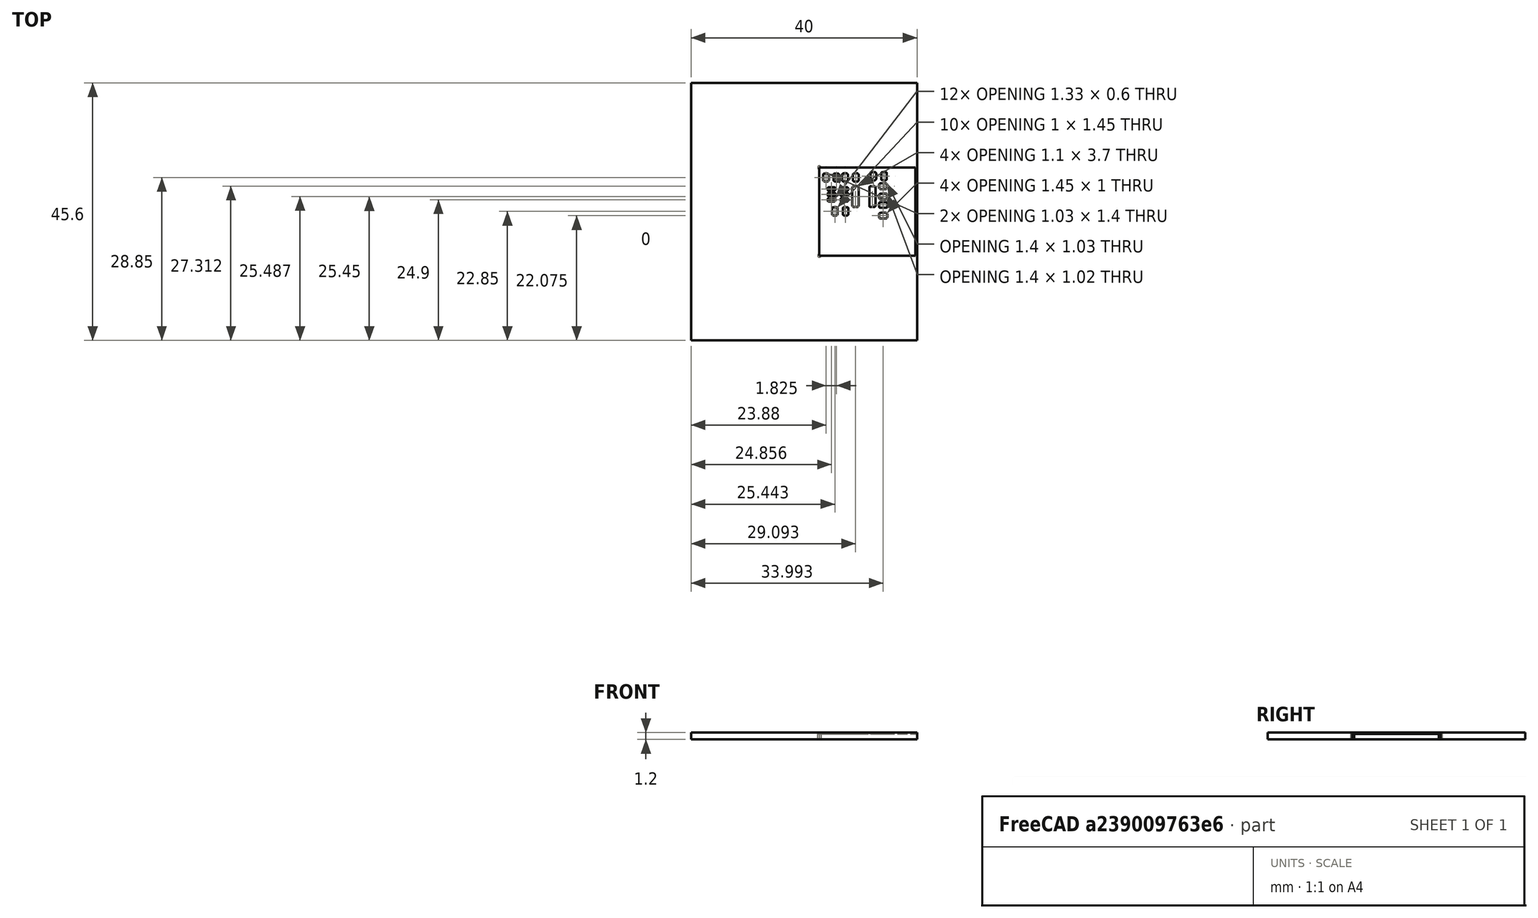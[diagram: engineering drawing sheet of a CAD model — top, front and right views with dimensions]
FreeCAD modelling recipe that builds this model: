
FCSTD DOCUMENT  (FreeCAD 1.0R39319 (Git))
Label: stencil
License: All rights reserved
LicenseURL: https://en.wikipedia.org/wiki/All_rights_reserved
objects: Sketcher::SketchObject×3, Part::Extrusion×3, Part::Box×1, Part::MultiFuse×1
note: 11 computed .brp shape members not serialized (recipe doc carries the construction recipe); baked Part::Feature solids carry a one-line shape summary decoded from their .brp

FEATURE [Part::Box] Box  label="Cover"
  AttacherType = Attacher::AttachEngine3D
  Height = 0.2
  Length = 2
  Placement = pos=(146.75,-81,0) rot=(0,0,1;0rad)
  Width = 17
FEATURE [Sketcher::SketchObject] Sketch
  ArcFitTolerance = 1e-06
  FullyConstrained = false
  MakeInternals = false
  sketch-geometry (284):
    g0: BSplineCurve PolesCount=2 KnotsCount=2 Degree=1 IsPeriodic=0
    g1: BSplineCurve PolesCount=2 KnotsCount=2 Degree=1 IsPeriodic=0
    g2: BSplineCurve PolesCount=2 KnotsCount=2 Degree=1 IsPeriodic=0
    g3: BSplineCurve PolesCount=2 KnotsCount=2 Degree=1 IsPeriodic=0
    g4: BSplineCurve PolesCount=2 KnotsCount=2 Degree=1 IsPeriodic=0
    g5: BSplineCurve PolesCount=2 KnotsCount=2 Degree=1 IsPeriodic=0
    g6: BSplineCurve PolesCount=2 KnotsCount=2 Degree=1 IsPeriodic=0
    g7: BSplineCurve PolesCount=2 KnotsCount=2 Degree=1 IsPeriodic=0
    g8: BSplineCurve PolesCount=2 KnotsCount=2 Degree=1 IsPeriodic=0
    g9: BSplineCurve PolesCount=2 KnotsCount=2 Degree=1 IsPeriodic=0
    g10: BSplineCurve PolesCount=2 KnotsCount=2 Degree=1 IsPeriodic=0
    g11: BSplineCurve PolesCount=2 KnotsCount=2 Degree=1 IsPeriodic=0
    g12: BSplineCurve PolesCount=2 KnotsCount=2 Degree=1 IsPeriodic=0
    g13: BSplineCurve PolesCount=2 KnotsCount=2 Degree=1 IsPeriodic=0
    g14: BSplineCurve PolesCount=2 KnotsCount=2 Degree=1 IsPeriodic=0
    g15: BSplineCurve PolesCount=2 KnotsCount=2 Degree=1 IsPeriodic=0
    g16: BSplineCurve PolesCount=2 KnotsCount=2 Degree=1 IsPeriodic=0
    g17: BSplineCurve PolesCount=2 KnotsCount=2 Degree=1 IsPeriodic=0
    g18: BSplineCurve PolesCount=2 KnotsCount=2 Degree=1 IsPeriodic=0
    g19: BSplineCurve PolesCount=2 KnotsCount=2 Degree=1 IsPeriodic=0
    g20: BSplineCurve PolesCount=2 KnotsCount=2 Degree=1 IsPeriodic=0
    g21: BSplineCurve PolesCount=2 KnotsCount=2 Degree=1 IsPeriodic=0
    g22: BSplineCurve PolesCount=2 KnotsCount=2 Degree=1 IsPeriodic=0
    g23: BSplineCurve PolesCount=2 KnotsCount=2 Degree=1 IsPeriodic=0
    g24: BSplineCurve PolesCount=2 KnotsCount=2 Degree=1 IsPeriodic=0
    g25: BSplineCurve PolesCount=2 KnotsCount=2 Degree=1 IsPeriodic=0
    g26: BSplineCurve PolesCount=2 KnotsCount=2 Degree=1 IsPeriodic=0
    g27: BSplineCurve PolesCount=2 KnotsCount=2 Degree=1 IsPeriodic=0
    g28: BSplineCurve PolesCount=2 KnotsCount=2 Degree=1 IsPeriodic=0
    g29: BSplineCurve PolesCount=2 KnotsCount=2 Degree=1 IsPeriodic=0
    g30: BSplineCurve PolesCount=2 KnotsCount=2 Degree=1 IsPeriodic=0
    g31: BSplineCurve PolesCount=2 KnotsCount=2 Degree=1 IsPeriodic=0
    g32: BSplineCurve PolesCount=2 KnotsCount=2 Degree=1 IsPeriodic=0
    g33: BSplineCurve PolesCount=2 KnotsCount=2 Degree=1 IsPeriodic=0
    g34: BSplineCurve PolesCount=2 KnotsCount=2 Degree=1 IsPeriodic=0
    g35: BSplineCurve PolesCount=2 KnotsCount=2 Degree=1 IsPeriodic=0
    g36: BSplineCurve PolesCount=2 KnotsCount=2 Degree=1 IsPeriodic=0
    g37: BSplineCurve PolesCount=2 KnotsCount=2 Degree=1 IsPeriodic=0
    g38: BSplineCurve PolesCount=2 KnotsCount=2 Degree=1 IsPeriodic=0
    g39: BSplineCurve PolesCount=2 KnotsCount=2 Degree=1 IsPeriodic=0
    g40: BSplineCurve PolesCount=2 KnotsCount=2 Degree=1 IsPeriodic=0
    g41: BSplineCurve PolesCount=2 KnotsCount=2 Degree=1 IsPeriodic=0
    g42: BSplineCurve PolesCount=2 KnotsCount=2 Degree=1 IsPeriodic=0
    g43: BSplineCurve PolesCount=2 KnotsCount=2 Degree=1 IsPeriodic=0
    g44: BSplineCurve PolesCount=2 KnotsCount=2 Degree=1 IsPeriodic=0
    g45: BSplineCurve PolesCount=2 KnotsCount=2 Degree=1 IsPeriodic=0
    g46: BSplineCurve PolesCount=2 KnotsCount=2 Degree=1 IsPeriodic=0
    g47: BSplineCurve PolesCount=2 KnotsCount=2 Degree=1 IsPeriodic=0
    g48: BSplineCurve PolesCount=2 KnotsCount=2 Degree=1 IsPeriodic=0
    g49: BSplineCurve PolesCount=2 KnotsCount=2 Degree=1 IsPeriodic=0
    g50: BSplineCurve PolesCount=2 KnotsCount=2 Degree=1 IsPeriodic=0
    g51: BSplineCurve PolesCount=2 KnotsCount=2 Degree=1 IsPeriodic=0
    g52: BSplineCurve PolesCount=2 KnotsCount=2 Degree=1 IsPeriodic=0
    g53: BSplineCurve PolesCount=2 KnotsCount=2 Degree=1 IsPeriodic=0
    g54: BSplineCurve PolesCount=2 KnotsCount=2 Degree=1 IsPeriodic=0
    g55: BSplineCurve PolesCount=2 KnotsCount=2 Degree=1 IsPeriodic=0
    g56: BSplineCurve PolesCount=2 KnotsCount=2 Degree=1 IsPeriodic=0
    g57: BSplineCurve PolesCount=2 KnotsCount=2 Degree=1 IsPeriodic=0
    g58: BSplineCurve PolesCount=2 KnotsCount=2 Degree=1 IsPeriodic=0
    g59: BSplineCurve PolesCount=2 KnotsCount=2 Degree=1 IsPeriodic=0
    g60: BSplineCurve PolesCount=2 KnotsCount=2 Degree=1 IsPeriodic=0
    g61: BSplineCurve PolesCount=2 KnotsCount=2 Degree=1 IsPeriodic=0
    g62: BSplineCurve PolesCount=2 KnotsCount=2 Degree=1 IsPeriodic=0
    g63: BSplineCurve PolesCount=2 KnotsCount=2 Degree=1 IsPeriodic=0
    g64: BSplineCurve PolesCount=2 KnotsCount=2 Degree=1 IsPeriodic=0
    g65: BSplineCurve PolesCount=2 KnotsCount=2 Degree=1 IsPeriodic=0
    g66: BSplineCurve PolesCount=2 KnotsCount=2 Degree=1 IsPeriodic=0
    g67: BSplineCurve PolesCount=2 KnotsCount=2 Degree=1 IsPeriodic=0
    g68: BSplineCurve PolesCount=2 KnotsCount=2 Degree=1 IsPeriodic=0
    g69: BSplineCurve PolesCount=2 KnotsCount=2 Degree=1 IsPeriodic=0
    g70: BSplineCurve PolesCount=2 KnotsCount=2 Degree=1 IsPeriodic=0
    g71: BSplineCurve PolesCount=2 KnotsCount=2 Degree=1 IsPeriodic=0
    g72: BSplineCurve PolesCount=2 KnotsCount=2 Degree=1 IsPeriodic=0
    g73: BSplineCurve PolesCount=2 KnotsCount=2 Degree=1 IsPeriodic=0
    g74: BSplineCurve PolesCount=2 KnotsCount=2 Degree=1 IsPeriodic=0
    g75: BSplineCurve PolesCount=2 KnotsCount=2 Degree=1 IsPeriodic=0
    g76: BSplineCurve PolesCount=2 KnotsCount=2 Degree=1 IsPeriodic=0
    g77: BSplineCurve PolesCount=2 KnotsCount=2 Degree=1 IsPeriodic=0
    g78: BSplineCurve PolesCount=2 KnotsCount=2 Degree=1 IsPeriodic=0
    g79: BSplineCurve PolesCount=2 KnotsCount=2 Degree=1 IsPeriodic=0
    g80: BSplineCurve PolesCount=2 KnotsCount=2 Degree=1 IsPeriodic=0
    g81: BSplineCurve PolesCount=2 KnotsCount=2 Degree=1 IsPeriodic=0
    g82: BSplineCurve PolesCount=2 KnotsCount=2 Degree=1 IsPeriodic=0
    g83: BSplineCurve PolesCount=2 KnotsCount=2 Degree=1 IsPeriodic=0
    g84: BSplineCurve PolesCount=2 KnotsCount=2 Degree=1 IsPeriodic=0
    g85: BSplineCurve PolesCount=2 KnotsCount=2 Degree=1 IsPeriodic=0
    g86: BSplineCurve PolesCount=2 KnotsCount=2 Degree=1 IsPeriodic=0
    g87: BSplineCurve PolesCount=2 KnotsCount=2 Degree=1 IsPeriodic=0
    g88: BSplineCurve PolesCount=2 KnotsCount=2 Degree=1 IsPeriodic=0
    g89: BSplineCurve PolesCount=2 KnotsCount=2 Degree=1 IsPeriodic=0
    g90: BSplineCurve PolesCount=2 KnotsCount=2 Degree=1 IsPeriodic=0
    g91: BSplineCurve PolesCount=2 KnotsCount=2 Degree=1 IsPeriodic=0
    g92: BSplineCurve PolesCount=2 KnotsCount=2 Degree=1 IsPeriodic=0
    g93: BSplineCurve PolesCount=2 KnotsCount=2 Degree=1 IsPeriodic=0
    g94: BSplineCurve PolesCount=2 KnotsCount=2 Degree=1 IsPeriodic=0
    g95: BSplineCurve PolesCount=2 KnotsCount=2 Degree=1 IsPeriodic=0
    g96: BSplineCurve PolesCount=2 KnotsCount=2 Degree=1 IsPeriodic=0
    g97: BSplineCurve PolesCount=2 KnotsCount=2 Degree=1 IsPeriodic=0
    g98: BSplineCurve PolesCount=2 KnotsCount=2 Degree=1 IsPeriodic=0
    g99: BSplineCurve PolesCount=2 KnotsCount=2 Degree=1 IsPeriodic=0
    g100: BSplineCurve PolesCount=2 KnotsCount=2 Degree=1 IsPeriodic=0
    g101: BSplineCurve PolesCount=2 KnotsCount=2 Degree=1 IsPeriodic=0
    g102: BSplineCurve PolesCount=2 KnotsCount=2 Degree=1 IsPeriodic=0
    g103: BSplineCurve PolesCount=2 KnotsCount=2 Degree=1 IsPeriodic=0
    g104: BSplineCurve PolesCount=2 KnotsCount=2 Degree=1 IsPeriodic=0
    g105: BSplineCurve PolesCount=2 KnotsCount=2 Degree=1 IsPeriodic=0
    g106: BSplineCurve PolesCount=2 KnotsCount=2 Degree=1 IsPeriodic=0
    g107: BSplineCurve PolesCount=2 KnotsCount=2 Degree=1 IsPeriodic=0
    g108: BSplineCurve PolesCount=2 KnotsCount=2 Degree=1 IsPeriodic=0
    g109: BSplineCurve PolesCount=2 KnotsCount=2 Degree=1 IsPeriodic=0
    g110: BSplineCurve PolesCount=2 KnotsCount=2 Degree=1 IsPeriodic=0
    g111: BSplineCurve PolesCount=2 KnotsCount=2 Degree=1 IsPeriodic=0
    g112: BSplineCurve PolesCount=2 KnotsCount=2 Degree=1 IsPeriodic=0
    g113: BSplineCurve PolesCount=2 KnotsCount=2 Degree=1 IsPeriodic=0
    g114: BSplineCurve PolesCount=2 KnotsCount=2 Degree=1 IsPeriodic=0
    g115: BSplineCurve PolesCount=2 KnotsCount=2 Degree=1 IsPeriodic=0
    g116: BSplineCurve PolesCount=2 KnotsCount=2 Degree=1 IsPeriodic=0
    g117: BSplineCurve PolesCount=2 KnotsCount=2 Degree=1 IsPeriodic=0
    g118: BSplineCurve PolesCount=2 KnotsCount=2 Degree=1 IsPeriodic=0
    g119: BSplineCurve PolesCount=2 KnotsCount=2 Degree=1 IsPeriodic=0
    g120: BSplineCurve PolesCount=2 KnotsCount=2 Degree=1 IsPeriodic=0
    g121: BSplineCurve PolesCount=2 KnotsCount=2 Degree=1 IsPeriodic=0
    g122: BSplineCurve PolesCount=2 KnotsCount=2 Degree=1 IsPeriodic=0
    g123: BSplineCurve PolesCount=2 KnotsCount=2 Degree=1 IsPeriodic=0
    g124: BSplineCurve PolesCount=2 KnotsCount=2 Degree=1 IsPeriodic=0
    g125: BSplineCurve PolesCount=2 KnotsCount=2 Degree=1 IsPeriodic=0
    g126: BSplineCurve PolesCount=2 KnotsCount=2 Degree=1 IsPeriodic=0
    g127: BSplineCurve PolesCount=2 KnotsCount=2 Degree=1 IsPeriodic=0
    g128: BSplineCurve PolesCount=2 KnotsCount=2 Degree=1 IsPeriodic=0
    g129: BSplineCurve PolesCount=2 KnotsCount=2 Degree=1 IsPeriodic=0
    g130: BSplineCurve PolesCount=2 KnotsCount=2 Degree=1 IsPeriodic=0
    g131: BSplineCurve PolesCount=2 KnotsCount=2 Degree=1 IsPeriodic=0
    g132: BSplineCurve PolesCount=2 KnotsCount=2 Degree=1 IsPeriodic=0
    g133: BSplineCurve PolesCount=2 KnotsCount=2 Degree=1 IsPeriodic=0
    g134: BSplineCurve PolesCount=2 KnotsCount=2 Degree=1 IsPeriodic=0
    g135: BSplineCurve PolesCount=2 KnotsCount=2 Degree=1 IsPeriodic=0
    g136: BSplineCurve PolesCount=2 KnotsCount=2 Degree=1 IsPeriodic=0
    g137: BSplineCurve PolesCount=2 KnotsCount=2 Degree=1 IsPeriodic=0
    g138: BSplineCurve PolesCount=2 KnotsCount=2 Degree=1 IsPeriodic=0
    g139: BSplineCurve PolesCount=2 KnotsCount=2 Degree=1 IsPeriodic=0
    g140: BSplineCurve PolesCount=2 KnotsCount=2 Degree=1 IsPeriodic=0
    g141: BSplineCurve PolesCount=2 KnotsCount=2 Degree=1 IsPeriodic=0
    g142: BSplineCurve PolesCount=2 KnotsCount=2 Degree=1 IsPeriodic=0
    g143: BSplineCurve PolesCount=2 KnotsCount=2 Degree=1 IsPeriodic=0
    g144: BSplineCurve PolesCount=2 KnotsCount=2 Degree=1 IsPeriodic=0
    g145: BSplineCurve PolesCount=2 KnotsCount=2 Degree=1 IsPeriodic=0
    g146: BSplineCurve PolesCount=2 KnotsCount=2 Degree=1 IsPeriodic=0
    g147: BSplineCurve PolesCount=2 KnotsCount=2 Degree=1 IsPeriodic=0
    g148: BSplineCurve PolesCount=2 KnotsCount=2 Degree=1 IsPeriodic=0
    g149: BSplineCurve PolesCount=2 KnotsCount=2 Degree=1 IsPeriodic=0
    g150: BSplineCurve PolesCount=2 KnotsCount=2 Degree=1 IsPeriodic=0
    g151: BSplineCurve PolesCount=2 KnotsCount=2 Degree=1 IsPeriodic=0
    g152: BSplineCurve PolesCount=2 KnotsCount=2 Degree=1 IsPeriodic=0
    g153: BSplineCurve PolesCount=2 KnotsCount=2 Degree=1 IsPeriodic=0
    g154: BSplineCurve PolesCount=2 KnotsCount=2 Degree=1 IsPeriodic=0
    g155: BSplineCurve PolesCount=2 KnotsCount=2 Degree=1 IsPeriodic=0
    g156: BSplineCurve PolesCount=2 KnotsCount=2 Degree=1 IsPeriodic=0
    g157: BSplineCurve PolesCount=2 KnotsCount=2 Degree=1 IsPeriodic=0
    g158: BSplineCurve PolesCount=2 KnotsCount=2 Degree=1 IsPeriodic=0
    g159: BSplineCurve PolesCount=2 KnotsCount=2 Degree=1 IsPeriodic=0
    g160: BSplineCurve PolesCount=2 KnotsCount=2 Degree=1 IsPeriodic=0
    g161: BSplineCurve PolesCount=2 KnotsCount=2 Degree=1 IsPeriodic=0
    g162: BSplineCurve PolesCount=2 KnotsCount=2 Degree=1 IsPeriodic=0
    g163: BSplineCurve PolesCount=2 KnotsCount=2 Degree=1 IsPeriodic=0
    g164: BSplineCurve PolesCount=2 KnotsCount=2 Degree=1 IsPeriodic=0
    g165: BSplineCurve PolesCount=2 KnotsCount=2 Degree=1 IsPeriodic=0
    g166: BSplineCurve PolesCount=2 KnotsCount=2 Degree=1 IsPeriodic=0
    g167: BSplineCurve PolesCount=2 KnotsCount=2 Degree=1 IsPeriodic=0
    g168: BSplineCurve PolesCount=2 KnotsCount=2 Degree=1 IsPeriodic=0
    g169: BSplineCurve PolesCount=2 KnotsCount=2 Degree=1 IsPeriodic=0
    g170: BSplineCurve PolesCount=2 KnotsCount=2 Degree=1 IsPeriodic=0
    g171: BSplineCurve PolesCount=2 KnotsCount=2 Degree=1 IsPeriodic=0
    g172: BSplineCurve PolesCount=2 KnotsCount=2 Degree=1 IsPeriodic=0
    g173: BSplineCurve PolesCount=2 KnotsCount=2 Degree=1 IsPeriodic=0
    g174: BSplineCurve PolesCount=2 KnotsCount=2 Degree=1 IsPeriodic=0
    g175: BSplineCurve PolesCount=2 KnotsCount=2 Degree=1 IsPeriodic=0
    g176: BSplineCurve PolesCount=2 KnotsCount=2 Degree=1 IsPeriodic=0
    g177: BSplineCurve PolesCount=2 KnotsCount=2 Degree=1 IsPeriodic=0
    g178: BSplineCurve PolesCount=2 KnotsCount=2 Degree=1 IsPeriodic=0
    g179: BSplineCurve PolesCount=2 KnotsCount=2 Degree=1 IsPeriodic=0
    g180: BSplineCurve PolesCount=2 KnotsCount=2 Degree=1 IsPeriodic=0
    g181: BSplineCurve PolesCount=2 KnotsCount=2 Degree=1 IsPeriodic=0
    g182: BSplineCurve PolesCount=2 KnotsCount=2 Degree=1 IsPeriodic=0
    g183: BSplineCurve PolesCount=2 KnotsCount=2 Degree=1 IsPeriodic=0
    g184: BSplineCurve PolesCount=2 KnotsCount=2 Degree=1 IsPeriodic=0
    g185: BSplineCurve PolesCount=2 KnotsCount=2 Degree=1 IsPeriodic=0
    g186: BSplineCurve PolesCount=2 KnotsCount=2 Degree=1 IsPeriodic=0
    g187: BSplineCurve PolesCount=2 KnotsCount=2 Degree=1 IsPeriodic=0
    g188: BSplineCurve PolesCount=2 KnotsCount=2 Degree=1 IsPeriodic=0
    g189: BSplineCurve PolesCount=2 KnotsCount=2 Degree=1 IsPeriodic=0
    g190: BSplineCurve PolesCount=2 KnotsCount=2 Degree=1 IsPeriodic=0
    g191: BSplineCurve PolesCount=2 KnotsCount=2 Degree=1 IsPeriodic=0
    g192: BSplineCurve PolesCount=2 KnotsCount=2 Degree=1 IsPeriodic=0
    g193: BSplineCurve PolesCount=2 KnotsCount=2 Degree=1 IsPeriodic=0
    g194: BSplineCurve PolesCount=2 KnotsCount=2 Degree=1 IsPeriodic=0
    g195: BSplineCurve PolesCount=2 KnotsCount=2 Degree=1 IsPeriodic=0
    g196: BSplineCurve PolesCount=2 KnotsCount=2 Degree=1 IsPeriodic=0
    g197: BSplineCurve PolesCount=2 KnotsCount=2 Degree=1 IsPeriodic=0
    g198: BSplineCurve PolesCount=2 KnotsCount=2 Degree=1 IsPeriodic=0
    g199: BSplineCurve PolesCount=2 KnotsCount=2 Degree=1 IsPeriodic=0
    g200: BSplineCurve PolesCount=2 KnotsCount=2 Degree=1 IsPeriodic=0
    g201: BSplineCurve PolesCount=2 KnotsCount=2 Degree=1 IsPeriodic=0
    g202: BSplineCurve PolesCount=2 KnotsCount=2 Degree=1 IsPeriodic=0
    g203: BSplineCurve PolesCount=2 KnotsCount=2 Degree=1 IsPeriodic=0
    g204: BSplineCurve PolesCount=2 KnotsCount=2 Degree=1 IsPeriodic=0
    g205: BSplineCurve PolesCount=2 KnotsCount=2 Degree=1 IsPeriodic=0
    g206: BSplineCurve PolesCount=2 KnotsCount=2 Degree=1 IsPeriodic=0
    g207: BSplineCurve PolesCount=2 KnotsCount=2 Degree=1 IsPeriodic=0
    g208: BSplineCurve PolesCount=2 KnotsCount=2 Degree=1 IsPeriodic=0
    g209: BSplineCurve PolesCount=2 KnotsCount=2 Degree=1 IsPeriodic=0
    g210: BSplineCurve PolesCount=2 KnotsCount=2 Degree=1 IsPeriodic=0
    g211: BSplineCurve PolesCount=2 KnotsCount=2 Degree=1 IsPeriodic=0
    g212: BSplineCurve PolesCount=2 KnotsCount=2 Degree=1 IsPeriodic=0
    g213: BSplineCurve PolesCount=2 KnotsCount=2 Degree=1 IsPeriodic=0
    g214: BSplineCurve PolesCount=2 KnotsCount=2 Degree=1 IsPeriodic=0
    g215: BSplineCurve PolesCount=2 KnotsCount=2 Degree=1 IsPeriodic=0
    g216: BSplineCurve PolesCount=2 KnotsCount=2 Degree=1 IsPeriodic=0
    g217: BSplineCurve PolesCount=2 KnotsCount=2 Degree=1 IsPeriodic=0
    g218: BSplineCurve PolesCount=2 KnotsCount=2 Degree=1 IsPeriodic=0
    g219: BSplineCurve PolesCount=2 KnotsCount=2 Degree=1 IsPeriodic=0
    g220: BSplineCurve PolesCount=2 KnotsCount=2 Degree=1 IsPeriodic=0
    g221: BSplineCurve PolesCount=2 KnotsCount=2 Degree=1 IsPeriodic=0
    g222: BSplineCurve PolesCount=2 KnotsCount=2 Degree=1 IsPeriodic=0
    g223: BSplineCurve PolesCount=2 KnotsCount=2 Degree=1 IsPeriodic=0
    g224: BSplineCurve PolesCount=2 KnotsCount=2 Degree=1 IsPeriodic=0
    g225: BSplineCurve PolesCount=2 KnotsCount=2 Degree=1 IsPeriodic=0
    g226: BSplineCurve PolesCount=2 KnotsCount=2 Degree=1 IsPeriodic=0
    g227: BSplineCurve PolesCount=2 KnotsCount=2 Degree=1 IsPeriodic=0
    g228: BSplineCurve PolesCount=2 KnotsCount=2 Degree=1 IsPeriodic=0
    g229: BSplineCurve PolesCount=2 KnotsCount=2 Degree=1 IsPeriodic=0
    g230: BSplineCurve PolesCount=2 KnotsCount=2 Degree=1 IsPeriodic=0
    g231: BSplineCurve PolesCount=2 KnotsCount=2 Degree=1 IsPeriodic=0
    g232: BSplineCurve PolesCount=2 KnotsCount=2 Degree=1 IsPeriodic=0
    g233: BSplineCurve PolesCount=2 KnotsCount=2 Degree=1 IsPeriodic=0
    g234: BSplineCurve PolesCount=2 KnotsCount=2 Degree=1 IsPeriodic=0
    g235: BSplineCurve PolesCount=2 KnotsCount=2 Degree=1 IsPeriodic=0
    g236: BSplineCurve PolesCount=2 KnotsCount=2 Degree=1 IsPeriodic=0
    g237: BSplineCurve PolesCount=2 KnotsCount=2 Degree=1 IsPeriodic=0
    g238: BSplineCurve PolesCount=2 KnotsCount=2 Degree=1 IsPeriodic=0
    g239: BSplineCurve PolesCount=2 KnotsCount=2 Degree=1 IsPeriodic=0
    g240: BSplineCurve PolesCount=2 KnotsCount=2 Degree=1 IsPeriodic=0
    g241: BSplineCurve PolesCount=2 KnotsCount=2 Degree=1 IsPeriodic=0
    g242: BSplineCurve PolesCount=2 KnotsCount=2 Degree=1 IsPeriodic=0
    g243: BSplineCurve PolesCount=2 KnotsCount=2 Degree=1 IsPeriodic=0
    g244: BSplineCurve PolesCount=2 KnotsCount=2 Degree=1 IsPeriodic=0
    g245: BSplineCurve PolesCount=2 KnotsCount=2 Degree=1 IsPeriodic=0
    g246: BSplineCurve PolesCount=2 KnotsCount=2 Degree=1 IsPeriodic=0
    g247: BSplineCurve PolesCount=2 KnotsCount=2 Degree=1 IsPeriodic=0
    g248: BSplineCurve PolesCount=2 KnotsCount=2 Degree=1 IsPeriodic=0
    g249: BSplineCurve PolesCount=2 KnotsCount=2 Degree=1 IsPeriodic=0
    g250: BSplineCurve PolesCount=2 KnotsCount=2 Degree=1 IsPeriodic=0
    g251: BSplineCurve PolesCount=2 KnotsCount=2 Degree=1 IsPeriodic=0
    g252: BSplineCurve PolesCount=2 KnotsCount=2 Degree=1 IsPeriodic=0
    g253: BSplineCurve PolesCount=2 KnotsCount=2 Degree=1 IsPeriodic=0
    g254: BSplineCurve PolesCount=2 KnotsCount=2 Degree=1 IsPeriodic=0
    g255: BSplineCurve PolesCount=2 KnotsCount=2 Degree=1 IsPeriodic=0
    g256: BSplineCurve PolesCount=2 KnotsCount=2 Degree=1 IsPeriodic=0
    g257: BSplineCurve PolesCount=2 KnotsCount=2 Degree=1 IsPeriodic=0
    g258: BSplineCurve PolesCount=2 KnotsCount=2 Degree=1 IsPeriodic=0
    g259: BSplineCurve PolesCount=2 KnotsCount=2 Degree=1 IsPeriodic=0
    g260: BSplineCurve PolesCount=2 KnotsCount=2 Degree=1 IsPeriodic=0
    g261: BSplineCurve PolesCount=2 KnotsCount=2 Degree=1 IsPeriodic=0
    g262: BSplineCurve PolesCount=2 KnotsCount=2 Degree=1 IsPeriodic=0
    g263: BSplineCurve PolesCount=2 KnotsCount=2 Degree=1 IsPeriodic=0
    g264: BSplineCurve PolesCount=2 KnotsCount=2 Degree=1 IsPeriodic=0
    g265: BSplineCurve PolesCount=2 KnotsCount=2 Degree=1 IsPeriodic=0
    g266: BSplineCurve PolesCount=2 KnotsCount=2 Degree=1 IsPeriodic=0
    g267: BSplineCurve PolesCount=2 KnotsCount=2 Degree=1 IsPeriodic=0
    g268: BSplineCurve PolesCount=2 KnotsCount=2 Degree=1 IsPeriodic=0
    g269: BSplineCurve PolesCount=2 KnotsCount=2 Degree=1 IsPeriodic=0
    g270: BSplineCurve PolesCount=2 KnotsCount=2 Degree=1 IsPeriodic=0
    g271: BSplineCurve PolesCount=2 KnotsCount=2 Degree=1 IsPeriodic=0
    g272: BSplineCurve PolesCount=2 KnotsCount=2 Degree=1 IsPeriodic=0
    g273: BSplineCurve PolesCount=2 KnotsCount=2 Degree=1 IsPeriodic=0
    g274: BSplineCurve PolesCount=2 KnotsCount=2 Degree=1 IsPeriodic=0
    g275: BSplineCurve PolesCount=2 KnotsCount=2 Degree=1 IsPeriodic=0
    g276: BSplineCurve PolesCount=2 KnotsCount=2 Degree=1 IsPeriodic=0
    g277: BSplineCurve PolesCount=2 KnotsCount=2 Degree=1 IsPeriodic=0
    g278: BSplineCurve PolesCount=2 KnotsCount=2 Degree=1 IsPeriodic=0
    g279: BSplineCurve PolesCount=2 KnotsCount=2 Degree=1 IsPeriodic=0
    g280: LineSegment StartX=148.35 StartY=-64.7 StartZ=0 EndX=148.35 EndY=-80.3 EndZ=0
    g281: LineSegment StartX=148.35 StartY=-80.3 StartZ=0 EndX=165.65 EndY=-80.3 EndZ=0
    g282: LineSegment StartX=165.65 StartY=-80.3 StartZ=0 EndX=165.65 EndY=-64.7 EndZ=0
    g283: LineSegment StartX=165.65 StartY=-64.7 StartZ=0 EndX=148.35 EndY=-64.7 EndZ=0
  constraints (292):
    c: Coincident(g0,g1)
    c: Coincident(g1,g2)
    c: Coincident(g2,g3)
    c: Coincident(g3,g4)
    c: Coincident(g4,g5)
    c: Coincident(g5,g6)
    c: Coincident(g6,g7)
    c: Coincident(g7,g8)
    c: Coincident(g8,g9)
    c: Coincident(g9,g10)
    c: Coincident(g10,g11)
    c: Coincident(g11,g12)
    c: Coincident(g12,g13)
    c: Coincident(g13,g14)
    c: Coincident(g14,g15)
    c: Coincident(g15,g16)
    c: Coincident(g16,g17)
    c: Coincident(g17,g18)
    c: Coincident(g18,g19)
    c: Coincident(g19,g0)
    c: Coincident(g20,g21)
    c: Coincident(g21,g22)
    c: Coincident(g22,g23)
    c: Coincident(g23,g24)
    c: Coincident(g24,g25)
    c: Coincident(g25,g26)
    c: Coincident(g26,g27)
    c: Coincident(g27,g28)
    c: Coincident(g28,g29)
    c: Coincident(g29,g30)
    c: Coincident(g30,g31)
    c: Coincident(g31,g32)
    c: Coincident(g32,g33)
    c: Coincident(g33,g34)
    c: Coincident(g34,g35)
    c: Coincident(g35,g36)
    c: Coincident(g36,g37)
    c: Coincident(g37,g38)
    c: Coincident(g38,g39)
    c: Coincident(g39,g20)
    c: Coincident(g40,g41)
    c: Coincident(g41,g42)
    c: Coincident(g42,g43)
    c: Coincident(g43,g44)
    c: Coincident(g44,g45)
    c: Coincident(g45,g46)
    c: Coincident(g46,g47)
    c: Coincident(g47,g48)
    c: Coincident(g48,g49)
    c: Coincident(g49,g50)
    c: Coincident(g50,g51)
    c: Coincident(g51,g52)
    c: Coincident(g52,g53)
    c: Coincident(g53,g54)
    c: Coincident(g54,g55)
    c: Coincident(g55,g56)
    c: Coincident(g56,g57)
    c: Coincident(g57,g58)
    c: Coincident(g58,g59)
    c: Coincident(g59,g40)
    c: Coincident(g60,g61)
    c: Coincident(g61,g62)
    c: Coincident(g62,g63)
    c: Coincident(g63,g64)
    c: Coincident(g64,g65)
    c: Coincident(g65,g66)
    c: Coincident(g66,g67)
    c: Coincident(g67,g68)
    c: Coincident(g68,g69)
    c: Coincident(g69,g70)
    c: Coincident(g70,g71)
    c: Coincident(g71,g72)
    c: Coincident(g72,g73)
    c: Coincident(g73,g74)
    c: Coincident(g74,g75)
    c: Coincident(g75,g76)
    c: Coincident(g76,g77)
    c: Coincident(g77,g78)
    c: Coincident(g78,g79)
    c: Coincident(g79,g60)
    c: Coincident(g80,g81)
    c: Coincident(g81,g82)
    c: Coincident(g82,g83)
    c: Coincident(g83,g84)
    c: Coincident(g84,g85)
    c: Coincident(g85,g86)
    c: Coincident(g86,g87)
    c: Coincident(g87,g88)
    c: Coincident(g88,g89)
    c: Coincident(g89,g90)
    c: Coincident(g90,g91)
    c: Coincident(g91,g92)
    c: Coincident(g92,g93)
    c: Coincident(g93,g94)
    c: Coincident(g94,g95)
    c: Coincident(g95,g96)
    c: Coincident(g96,g97)
    c: Coincident(g97,g98)
    c: Coincident(g98,g99)
    c: Coincident(g99,g80)
    c: Coincident(g100,g101)
    c: Coincident(g101,g102)
    c: Coincident(g102,g103)
    c: Coincident(g103,g104)
    c: Coincident(g104,g105)
    c: Coincident(g105,g106)
    c: Coincident(g106,g107)
    c: Coincident(g107,g108)
    c: Coincident(g108,g109)
    c: Coincident(g109,g110)
    c: Coincident(g110,g111)
    c: Coincident(g111,g112)
    c: Coincident(g112,g113)
    c: Coincident(g113,g114)
    c: Coincident(g114,g115)
    c: Coincident(g115,g116)
    c: Coincident(g116,g117)
    c: Coincident(g117,g118)
    c: Coincident(g118,g119)
    c: Coincident(g119,g100)
    c: Coincident(g120,g121)
    c: Coincident(g121,g122)
    c: Coincident(g122,g123)
    c: Coincident(g123,g124)
    c: Coincident(g124,g125)
    c: Coincident(g125,g126)
    c: Coincident(g126,g127)
    c: Coincident(g127,g128)
    c: Coincident(g128,g129)
    c: Coincident(g129,g130)
    c: Coincident(g130,g131)
    c: Coincident(g131,g132)
    c: Coincident(g132,g133)
    c: Coincident(g133,g134)
    c: Coincident(g134,g135)
    c: Coincident(g135,g136)
    c: Coincident(g136,g137)
    c: Coincident(g137,g138)
    c: Coincident(g138,g139)
    c: Coincident(g139,g120)
    c: Coincident(g140,g141)
    c: Coincident(g141,g142)
    c: Coincident(g142,g143)
    c: Coincident(g143,g144)
    c: Coincident(g144,g145)
    c: Coincident(g145,g146)
    c: Coincident(g146,g147)
    c: Coincident(g147,g148)
    c: Coincident(g148,g149)
    c: Coincident(g149,g150)
    c: Coincident(g150,g151)
    c: Coincident(g151,g152)
    c: Coincident(g152,g153)
    c: Coincident(g153,g154)
    c: Coincident(g154,g155)
    c: Coincident(g155,g156)
    c: Coincident(g156,g157)
    c: Coincident(g157,g158)
    c: Coincident(g158,g159)
    c: Coincident(g159,g140)
    c: Coincident(g160,g161)
    c: Coincident(g161,g162)
    c: Coincident(g162,g163)
    c: Coincident(g163,g164)
    c: Coincident(g164,g165)
    c: Coincident(g165,g166)
    c: Coincident(g166,g167)
    c: Coincident(g167,g168)
    c: Coincident(g168,g169)
    c: Coincident(g169,g170)
    c: Coincident(g170,g171)
    c: Coincident(g171,g172)
    c: Coincident(g172,g173)
    c: Coincident(g173,g174)
    c: Coincident(g174,g175)
    c: Coincident(g175,g176)
    c: Coincident(g176,g177)
    c: Coincident(g177,g178)
    c: Coincident(g178,g179)
    c: Coincident(g179,g160)
    c: Coincident(g180,g181)
    c: Coincident(g181,g182)
    c: Coincident(g182,g183)
    c: Coincident(g183,g184)
    c: Coincident(g184,g185)
    c: Coincident(g185,g186)
    c: Coincident(g186,g187)
    c: Coincident(g187,g188)
    c: Coincident(g188,g189)
    c: Coincident(g189,g190)
    c: Coincident(g190,g191)
    c: Coincident(g191,g192)
    c: Coincident(g192,g193)
    c: Coincident(g193,g194)
    c: Coincident(g194,g195)
    c: Coincident(g195,g196)
    c: Coincident(g196,g197)
    c: Coincident(g197,g198)
    c: Coincident(g198,g199)
    c: Coincident(g199,g180)
    c: Coincident(g200,g201)
    c: Coincident(g201,g202)
    c: Coincident(g202,g203)
    c: Coincident(g203,g204)
    c: Coincident(g204,g205)
    c: Coincident(g205,g206)
    c: Coincident(g206,g207)
    c: Coincident(g207,g208)
    c: Coincident(g208,g209)
    c: Coincident(g209,g210)
    c: Coincident(g210,g211)
    c: Coincident(g211,g212)
    c: Coincident(g212,g213)
    c: Coincident(g213,g214)
    c: Coincident(g214,g215)
    c: Coincident(g215,g216)
    c: Coincident(g216,g217)
    c: Coincident(g217,g218)
    c: Coincident(g218,g219)
    c: Coincident(g219,g200)
    c: Coincident(g220,g221)
    c: Coincident(g221,g222)
    c: Coincident(g222,g223)
    c: Coincident(g223,g224)
    c: Coincident(g224,g225)
    c: Coincident(g225,g226)
    c: Coincident(g226,g227)
    c: Coincident(g227,g228)
    c: Coincident(g228,g229)
    c: Coincident(g229,g230)
    c: Coincident(g230,g231)
    c: Coincident(g231,g232)
    c: Coincident(g232,g233)
    c: Coincident(g233,g234)
    c: Coincident(g234,g235)
    c: Coincident(g235,g236)
    c: Coincident(g236,g237)
    c: Coincident(g237,g238)
    c: Coincident(g238,g239)
    c: Coincident(g239,g220)
    c: Coincident(g240,g241)
    c: Coincident(g241,g242)
    c: Coincident(g242,g243)
    c: Coincident(g243,g244)
    c: Coincident(g244,g245)
    c: Coincident(g245,g246)
    c: Coincident(g246,g247)
    c: Coincident(g247,g248)
    c: Coincident(g248,g249)
    c: Coincident(g249,g250)
    c: Coincident(g250,g251)
    c: Coincident(g251,g252)
    c: Coincident(g252,g253)
    c: Coincident(g253,g254)
    c: Coincident(g254,g255)
    c: Coincident(g255,g256)
    c: Coincident(g256,g257)
    c: Coincident(g257,g258)
    c: Coincident(g258,g259)
    c: Coincident(g259,g240)
    c: Coincident(g260,g261)
    c: Coincident(g261,g262)
    c: Coincident(g262,g263)
    c: Coincident(g263,g264)
    c: Coincident(g264,g265)
    c: Coincident(g265,g266)
    c: Coincident(g266,g267)
    c: Coincident(g267,g268)
    c: Coincident(g268,g269)
    c: Coincident(g269,g270)
    c: Coincident(g270,g271)
    c: Coincident(g271,g272)
    c: Coincident(g272,g273)
    c: Coincident(g273,g274)
    c: Coincident(g274,g275)
    c: Coincident(g275,g276)
    c: Coincident(g276,g277)
    c: Coincident(g277,g278)
    c: Coincident(g278,g279)
    c: Coincident(g279,g260)
    c: Coincident(g280,g281)
    c: Coincident(g281,g282)
    c: Coincident(g282,g283)
    c: Coincident(g283,g280)
    c: Vertical(g280)
    c: Vertical(g282)
    c: Horizontal(g281)
    c: Horizontal(g283)
    c: DistanceY(g282,g282) = 15.6
    c: DistanceX(g281,g281) = 17.3
    c: DistanceY(g280) = -64.7
    c: DistanceX(g280) = 148.35
FEATURE [Part::Extrusion] Extrude  label="PCB-fix"
  Base = -> Sketch
  Dir = (0,0,1)
  DirMode = 2
  FaceMakerClass = Part::FaceMakerBullseye
  FaceMakerMode = 3
  LengthFwd = 0.2
  LengthRev = 0
  Solid = true
  Symmetric = false
FEATURE [Sketcher::SketchObject] Sketch001
  ArcFitTolerance = 1e-06
  AttachmentSupport = -> [Extrude]
  ExternalGeometry = -> [Extrude]
  FullyConstrained = true
  MakeInternals = false
  MapMode = 5
  Placement = pos=(0,0,0.2) rot=(0,0,1;0rad)
  sketch-geometry (10):
    g0: ArcOfCircle CenterX=148.35 CenterY=-64.7 CenterZ=0 NormalX=0 NormalY=0 NormalZ=1 AngleXU=0 Radius=0.3 StartAngle=3.482e-13 EndAngle=4.71239
    g1: ArcOfCircle CenterX=148.35 CenterY=-80.3 CenterZ=0 NormalX=0 NormalY=0 NormalZ=1 AngleXU=0 Radius=0.3 StartAngle=1.5708 EndAngle=6.28319
    g2: LineSegment StartX=148.35 StartY=-65 StartZ=0 EndX=148.35 EndY=-80 EndZ=0
    g3: LineSegment StartX=148.65 StartY=-80.3 StartZ=0 EndX=165.65 EndY=-80.3 EndZ=0
    g4: LineSegment StartX=148.65 StartY=-64.7 StartZ=0 EndX=165.65 EndY=-64.7 EndZ=0
    g5: LineSegment StartX=165.65 StartY=-64.7 StartZ=0 EndX=165.65 EndY=-49.7 EndZ=0
    g6: LineSegment StartX=165.65 StartY=-49.7 StartZ=0 EndX=125.65 EndY=-49.7 EndZ=0
    g7: LineSegment StartX=165.65 StartY=-80.3 StartZ=0 EndX=165.65 EndY=-95.3 EndZ=0
    g8: LineSegment StartX=165.65 StartY=-95.3 StartZ=0 EndX=125.65 EndY=-95.3 EndZ=0
    g9: LineSegment StartX=125.65 StartY=-95.3 StartZ=0 EndX=125.65 EndY=-49.7 EndZ=0
  constraints (28):
    c: Coincident(g0,g-8)
    c: PointOnObject(g0,g-8)
    c: PointOnObject(g0,g-7)
    c: Coincident(g1,g-9)
    c: PointOnObject(g1,g-9)
    c: PointOnObject(g1,g-8)
    c: Coincident(g2,g0)
    c: Coincident(g2,g1)
    c: Coincident(g3,g1)
    c: Coincident(g3,g-9)
    c: Coincident(g4,g0)
    c: Coincident(g4,g-7)
    c: Coincident(g5,g4)
    c: Vertical(g5)
    c: Coincident(g6,g5)
    c: Horizontal(g6)
    c: Coincident(g7,g3)
    c: Vertical(g7)
    c: Coincident(g8,g7)
    c: Horizontal(g8)
    c: Coincident(g9,g8)
    c: Coincident(g9,g6)
    c: Vertical(g9)
    c: Equal(g5,g7)
    c: DistanceY(g5,g5) = 15
    c: DistanceX(g6,g6) = 40
    c: Radius(g0) = 0.3
    c: Radius(g1) = 0.3
FEATURE [Part::Extrusion] Extrude001  label="Holder"
  Base = -> Sketch001
  Dir = (0,0,1)
  DirMode = 2
  FaceMakerClass = Part::FaceMakerBullseye
  FaceMakerMode = 3
  LengthFwd = -1.2
  LengthRev = 0
  Solid = true
  Symmetric = false
FEATURE [Sketcher::SketchObject] Sketch002
  ArcFitTolerance = 1e-06
  FullyConstrained = false
  MakeInternals = false
  Placement = pos=(0,0,0) rot=(0,0,-1;3.14159rad)
  sketch-geometry (404):
    g0: BSplineCurve PolesCount=2 KnotsCount=2 Degree=1 IsPeriodic=0
    g1: BSplineCurve PolesCount=2 KnotsCount=2 Degree=1 IsPeriodic=0
    g2: BSplineCurve PolesCount=2 KnotsCount=2 Degree=1 IsPeriodic=0
    g3: BSplineCurve PolesCount=2 KnotsCount=2 Degree=1 IsPeriodic=0
    g4: BSplineCurve PolesCount=2 KnotsCount=2 Degree=1 IsPeriodic=0
    g5: BSplineCurve PolesCount=2 KnotsCount=2 Degree=1 IsPeriodic=0
    g6: BSplineCurve PolesCount=2 KnotsCount=2 Degree=1 IsPeriodic=0
    g7: BSplineCurve PolesCount=2 KnotsCount=2 Degree=1 IsPeriodic=0
    g8: BSplineCurve PolesCount=2 KnotsCount=2 Degree=1 IsPeriodic=0
    g9: BSplineCurve PolesCount=2 KnotsCount=2 Degree=1 IsPeriodic=0
    g10: BSplineCurve PolesCount=2 KnotsCount=2 Degree=1 IsPeriodic=0
    g11: BSplineCurve PolesCount=2 KnotsCount=2 Degree=1 IsPeriodic=0
    g12: BSplineCurve PolesCount=2 KnotsCount=2 Degree=1 IsPeriodic=0
    g13: BSplineCurve PolesCount=2 KnotsCount=2 Degree=1 IsPeriodic=0
    g14: BSplineCurve PolesCount=2 KnotsCount=2 Degree=1 IsPeriodic=0
    g15: BSplineCurve PolesCount=2 KnotsCount=2 Degree=1 IsPeriodic=0
    g16: BSplineCurve PolesCount=2 KnotsCount=2 Degree=1 IsPeriodic=0
    g17: BSplineCurve PolesCount=2 KnotsCount=2 Degree=1 IsPeriodic=0
    g18: BSplineCurve PolesCount=2 KnotsCount=2 Degree=1 IsPeriodic=0
    g19: BSplineCurve PolesCount=2 KnotsCount=2 Degree=1 IsPeriodic=0
    g20: BSplineCurve PolesCount=2 KnotsCount=2 Degree=1 IsPeriodic=0
    g21: BSplineCurve PolesCount=2 KnotsCount=2 Degree=1 IsPeriodic=0
    g22: BSplineCurve PolesCount=2 KnotsCount=2 Degree=1 IsPeriodic=0
    g23: BSplineCurve PolesCount=2 KnotsCount=2 Degree=1 IsPeriodic=0
    g24: BSplineCurve PolesCount=2 KnotsCount=2 Degree=1 IsPeriodic=0
    g25: BSplineCurve PolesCount=2 KnotsCount=2 Degree=1 IsPeriodic=0
    g26: BSplineCurve PolesCount=2 KnotsCount=2 Degree=1 IsPeriodic=0
    g27: BSplineCurve PolesCount=2 KnotsCount=2 Degree=1 IsPeriodic=0
    g28: BSplineCurve PolesCount=2 KnotsCount=2 Degree=1 IsPeriodic=0
    g29: BSplineCurve PolesCount=2 KnotsCount=2 Degree=1 IsPeriodic=0
    g30: BSplineCurve PolesCount=2 KnotsCount=2 Degree=1 IsPeriodic=0
    g31: BSplineCurve PolesCount=2 KnotsCount=2 Degree=1 IsPeriodic=0
    g32: BSplineCurve PolesCount=2 KnotsCount=2 Degree=1 IsPeriodic=0
    g33: BSplineCurve PolesCount=2 KnotsCount=2 Degree=1 IsPeriodic=0
    g34: BSplineCurve PolesCount=2 KnotsCount=2 Degree=1 IsPeriodic=0
    g35: BSplineCurve PolesCount=2 KnotsCount=2 Degree=1 IsPeriodic=0
    g36: BSplineCurve PolesCount=2 KnotsCount=2 Degree=1 IsPeriodic=0
    g37: BSplineCurve PolesCount=2 KnotsCount=2 Degree=1 IsPeriodic=0
    g38: BSplineCurve PolesCount=2 KnotsCount=2 Degree=1 IsPeriodic=0
    g39: BSplineCurve PolesCount=2 KnotsCount=2 Degree=1 IsPeriodic=0
    g40: BSplineCurve PolesCount=2 KnotsCount=2 Degree=1 IsPeriodic=0
    g41: BSplineCurve PolesCount=2 KnotsCount=2 Degree=1 IsPeriodic=0
    g42: BSplineCurve PolesCount=2 KnotsCount=2 Degree=1 IsPeriodic=0
    g43: BSplineCurve PolesCount=2 KnotsCount=2 Degree=1 IsPeriodic=0
    g44: BSplineCurve PolesCount=2 KnotsCount=2 Degree=1 IsPeriodic=0
    g45: BSplineCurve PolesCount=2 KnotsCount=2 Degree=1 IsPeriodic=0
    g46: BSplineCurve PolesCount=2 KnotsCount=2 Degree=1 IsPeriodic=0
    g47: BSplineCurve PolesCount=2 KnotsCount=2 Degree=1 IsPeriodic=0
    g48: BSplineCurve PolesCount=2 KnotsCount=2 Degree=1 IsPeriodic=0
    g49: BSplineCurve PolesCount=2 KnotsCount=2 Degree=1 IsPeriodic=0
    g50: BSplineCurve PolesCount=2 KnotsCount=2 Degree=1 IsPeriodic=0
    g51: BSplineCurve PolesCount=2 KnotsCount=2 Degree=1 IsPeriodic=0
    g52: BSplineCurve PolesCount=2 KnotsCount=2 Degree=1 IsPeriodic=0
    g53: BSplineCurve PolesCount=2 KnotsCount=2 Degree=1 IsPeriodic=0
    g54: BSplineCurve PolesCount=2 KnotsCount=2 Degree=1 IsPeriodic=0
    g55: BSplineCurve PolesCount=2 KnotsCount=2 Degree=1 IsPeriodic=0
    g56: BSplineCurve PolesCount=2 KnotsCount=2 Degree=1 IsPeriodic=0
    g57: BSplineCurve PolesCount=2 KnotsCount=2 Degree=1 IsPeriodic=0
    g58: BSplineCurve PolesCount=2 KnotsCount=2 Degree=1 IsPeriodic=0
    g59: BSplineCurve PolesCount=2 KnotsCount=2 Degree=1 IsPeriodic=0
    g60: BSplineCurve PolesCount=2 KnotsCount=2 Degree=1 IsPeriodic=0
    g61: BSplineCurve PolesCount=2 KnotsCount=2 Degree=1 IsPeriodic=0
    g62: BSplineCurve PolesCount=2 KnotsCount=2 Degree=1 IsPeriodic=0
    g63: BSplineCurve PolesCount=2 KnotsCount=2 Degree=1 IsPeriodic=0
    g64: BSplineCurve PolesCount=2 KnotsCount=2 Degree=1 IsPeriodic=0
    g65: BSplineCurve PolesCount=2 KnotsCount=2 Degree=1 IsPeriodic=0
    g66: BSplineCurve PolesCount=2 KnotsCount=2 Degree=1 IsPeriodic=0
    g67: BSplineCurve PolesCount=2 KnotsCount=2 Degree=1 IsPeriodic=0
    g68: BSplineCurve PolesCount=2 KnotsCount=2 Degree=1 IsPeriodic=0
    g69: BSplineCurve PolesCount=2 KnotsCount=2 Degree=1 IsPeriodic=0
    g70: BSplineCurve PolesCount=2 KnotsCount=2 Degree=1 IsPeriodic=0
    g71: BSplineCurve PolesCount=2 KnotsCount=2 Degree=1 IsPeriodic=0
    g72: BSplineCurve PolesCount=2 KnotsCount=2 Degree=1 IsPeriodic=0
    g73: BSplineCurve PolesCount=2 KnotsCount=2 Degree=1 IsPeriodic=0
    g74: BSplineCurve PolesCount=2 KnotsCount=2 Degree=1 IsPeriodic=0
    g75: BSplineCurve PolesCount=2 KnotsCount=2 Degree=1 IsPeriodic=0
    g76: BSplineCurve PolesCount=2 KnotsCount=2 Degree=1 IsPeriodic=0
    g77: BSplineCurve PolesCount=2 KnotsCount=2 Degree=1 IsPeriodic=0
    g78: BSplineCurve PolesCount=2 KnotsCount=2 Degree=1 IsPeriodic=0
    g79: BSplineCurve PolesCount=2 KnotsCount=2 Degree=1 IsPeriodic=0
    g80: BSplineCurve PolesCount=2 KnotsCount=2 Degree=1 IsPeriodic=0
    g81: BSplineCurve PolesCount=2 KnotsCount=2 Degree=1 IsPeriodic=0
    g82: BSplineCurve PolesCount=2 KnotsCount=2 Degree=1 IsPeriodic=0
    g83: BSplineCurve PolesCount=2 KnotsCount=2 Degree=1 IsPeriodic=0
    g84: BSplineCurve PolesCount=2 KnotsCount=2 Degree=1 IsPeriodic=0
    g85: BSplineCurve PolesCount=2 KnotsCount=2 Degree=1 IsPeriodic=0
    g86: BSplineCurve PolesCount=2 KnotsCount=2 Degree=1 IsPeriodic=0
    g87: BSplineCurve PolesCount=2 KnotsCount=2 Degree=1 IsPeriodic=0
    g88: BSplineCurve PolesCount=2 KnotsCount=2 Degree=1 IsPeriodic=0
    g89: BSplineCurve PolesCount=2 KnotsCount=2 Degree=1 IsPeriodic=0
    g90: BSplineCurve PolesCount=2 KnotsCount=2 Degree=1 IsPeriodic=0
    g91: BSplineCurve PolesCount=2 KnotsCount=2 Degree=1 IsPeriodic=0
    g92: BSplineCurve PolesCount=2 KnotsCount=2 Degree=1 IsPeriodic=0
    g93: BSplineCurve PolesCount=2 KnotsCount=2 Degree=1 IsPeriodic=0
    g94: BSplineCurve PolesCount=2 KnotsCount=2 Degree=1 IsPeriodic=0
    g95: BSplineCurve PolesCount=2 KnotsCount=2 Degree=1 IsPeriodic=0
    g96: BSplineCurve PolesCount=2 KnotsCount=2 Degree=1 IsPeriodic=0
    g97: BSplineCurve PolesCount=2 KnotsCount=2 Degree=1 IsPeriodic=0
    g98: BSplineCurve PolesCount=2 KnotsCount=2 Degree=1 IsPeriodic=0
    g99: BSplineCurve PolesCount=2 KnotsCount=2 Degree=1 IsPeriodic=0
    g100: BSplineCurve PolesCount=2 KnotsCount=2 Degree=1 IsPeriodic=0
    g101: BSplineCurve PolesCount=2 KnotsCount=2 Degree=1 IsPeriodic=0
    g102: BSplineCurve PolesCount=2 KnotsCount=2 Degree=1 IsPeriodic=0
    g103: BSplineCurve PolesCount=2 KnotsCount=2 Degree=1 IsPeriodic=0
    g104: BSplineCurve PolesCount=2 KnotsCount=2 Degree=1 IsPeriodic=0
    g105: BSplineCurve PolesCount=2 KnotsCount=2 Degree=1 IsPeriodic=0
    g106: BSplineCurve PolesCount=2 KnotsCount=2 Degree=1 IsPeriodic=0
    g107: BSplineCurve PolesCount=2 KnotsCount=2 Degree=1 IsPeriodic=0
    g108: BSplineCurve PolesCount=2 KnotsCount=2 Degree=1 IsPeriodic=0
    g109: BSplineCurve PolesCount=2 KnotsCount=2 Degree=1 IsPeriodic=0
    g110: BSplineCurve PolesCount=2 KnotsCount=2 Degree=1 IsPeriodic=0
    g111: BSplineCurve PolesCount=2 KnotsCount=2 Degree=1 IsPeriodic=0
    g112: BSplineCurve PolesCount=2 KnotsCount=2 Degree=1 IsPeriodic=0
    g113: BSplineCurve PolesCount=2 KnotsCount=2 Degree=1 IsPeriodic=0
    g114: BSplineCurve PolesCount=2 KnotsCount=2 Degree=1 IsPeriodic=0
    g115: BSplineCurve PolesCount=2 KnotsCount=2 Degree=1 IsPeriodic=0
    g116: BSplineCurve PolesCount=2 KnotsCount=2 Degree=1 IsPeriodic=0
    g117: BSplineCurve PolesCount=2 KnotsCount=2 Degree=1 IsPeriodic=0
    g118: BSplineCurve PolesCount=2 KnotsCount=2 Degree=1 IsPeriodic=0
    g119: BSplineCurve PolesCount=2 KnotsCount=2 Degree=1 IsPeriodic=0
    g120: BSplineCurve PolesCount=2 KnotsCount=2 Degree=1 IsPeriodic=0
    g121: BSplineCurve PolesCount=2 KnotsCount=2 Degree=1 IsPeriodic=0
    g122: BSplineCurve PolesCount=2 KnotsCount=2 Degree=1 IsPeriodic=0
    g123: BSplineCurve PolesCount=2 KnotsCount=2 Degree=1 IsPeriodic=0
    g124: BSplineCurve PolesCount=2 KnotsCount=2 Degree=1 IsPeriodic=0
    g125: BSplineCurve PolesCount=2 KnotsCount=2 Degree=1 IsPeriodic=0
    g126: BSplineCurve PolesCount=2 KnotsCount=2 Degree=1 IsPeriodic=0
    g127: BSplineCurve PolesCount=2 KnotsCount=2 Degree=1 IsPeriodic=0
    g128: BSplineCurve PolesCount=2 KnotsCount=2 Degree=1 IsPeriodic=0
    g129: BSplineCurve PolesCount=2 KnotsCount=2 Degree=1 IsPeriodic=0
    g130: BSplineCurve PolesCount=2 KnotsCount=2 Degree=1 IsPeriodic=0
    g131: BSplineCurve PolesCount=2 KnotsCount=2 Degree=1 IsPeriodic=0
    g132: BSplineCurve PolesCount=2 KnotsCount=2 Degree=1 IsPeriodic=0
    g133: BSplineCurve PolesCount=2 KnotsCount=2 Degree=1 IsPeriodic=0
    g134: BSplineCurve PolesCount=2 KnotsCount=2 Degree=1 IsPeriodic=0
    g135: BSplineCurve PolesCount=2 KnotsCount=2 Degree=1 IsPeriodic=0
    g136: BSplineCurve PolesCount=2 KnotsCount=2 Degree=1 IsPeriodic=0
    g137: BSplineCurve PolesCount=2 KnotsCount=2 Degree=1 IsPeriodic=0
    g138: BSplineCurve PolesCount=2 KnotsCount=2 Degree=1 IsPeriodic=0
    g139: BSplineCurve PolesCount=2 KnotsCount=2 Degree=1 IsPeriodic=0
    g140: BSplineCurve PolesCount=2 KnotsCount=2 Degree=1 IsPeriodic=0
    g141: BSplineCurve PolesCount=2 KnotsCount=2 Degree=1 IsPeriodic=0
    g142: BSplineCurve PolesCount=2 KnotsCount=2 Degree=1 IsPeriodic=0
    g143: BSplineCurve PolesCount=2 KnotsCount=2 Degree=1 IsPeriodic=0
    g144: BSplineCurve PolesCount=2 KnotsCount=2 Degree=1 IsPeriodic=0
    g145: BSplineCurve PolesCount=2 KnotsCount=2 Degree=1 IsPeriodic=0
    g146: BSplineCurve PolesCount=2 KnotsCount=2 Degree=1 IsPeriodic=0
    g147: BSplineCurve PolesCount=2 KnotsCount=2 Degree=1 IsPeriodic=0
    g148: BSplineCurve PolesCount=2 KnotsCount=2 Degree=1 IsPeriodic=0
    g149: BSplineCurve PolesCount=2 KnotsCount=2 Degree=1 IsPeriodic=0
    g150: BSplineCurve PolesCount=2 KnotsCount=2 Degree=1 IsPeriodic=0
    g151: BSplineCurve PolesCount=2 KnotsCount=2 Degree=1 IsPeriodic=0
    g152: BSplineCurve PolesCount=2 KnotsCount=2 Degree=1 IsPeriodic=0
    g153: BSplineCurve PolesCount=2 KnotsCount=2 Degree=1 IsPeriodic=0
    g154: BSplineCurve PolesCount=2 KnotsCount=2 Degree=1 IsPeriodic=0
    g155: BSplineCurve PolesCount=2 KnotsCount=2 Degree=1 IsPeriodic=0
    g156: BSplineCurve PolesCount=2 KnotsCount=2 Degree=1 IsPeriodic=0
    g157: BSplineCurve PolesCount=2 KnotsCount=2 Degree=1 IsPeriodic=0
    g158: BSplineCurve PolesCount=2 KnotsCount=2 Degree=1 IsPeriodic=0
    g159: BSplineCurve PolesCount=2 KnotsCount=2 Degree=1 IsPeriodic=0
    g160: BSplineCurve PolesCount=2 KnotsCount=2 Degree=1 IsPeriodic=0
    g161: BSplineCurve PolesCount=2 KnotsCount=2 Degree=1 IsPeriodic=0
    g162: BSplineCurve PolesCount=2 KnotsCount=2 Degree=1 IsPeriodic=0
    g163: BSplineCurve PolesCount=2 KnotsCount=2 Degree=1 IsPeriodic=0
    g164: BSplineCurve PolesCount=2 KnotsCount=2 Degree=1 IsPeriodic=0
    g165: BSplineCurve PolesCount=2 KnotsCount=2 Degree=1 IsPeriodic=0
    g166: BSplineCurve PolesCount=2 KnotsCount=2 Degree=1 IsPeriodic=0
    g167: BSplineCurve PolesCount=2 KnotsCount=2 Degree=1 IsPeriodic=0
    g168: BSplineCurve PolesCount=2 KnotsCount=2 Degree=1 IsPeriodic=0
    g169: BSplineCurve PolesCount=2 KnotsCount=2 Degree=1 IsPeriodic=0
    g170: BSplineCurve PolesCount=2 KnotsCount=2 Degree=1 IsPeriodic=0
    g171: BSplineCurve PolesCount=2 KnotsCount=2 Degree=1 IsPeriodic=0
    g172: BSplineCurve PolesCount=2 KnotsCount=2 Degree=1 IsPeriodic=0
    g173: BSplineCurve PolesCount=2 KnotsCount=2 Degree=1 IsPeriodic=0
    g174: BSplineCurve PolesCount=2 KnotsCount=2 Degree=1 IsPeriodic=0
    g175: BSplineCurve PolesCount=2 KnotsCount=2 Degree=1 IsPeriodic=0
    g176: BSplineCurve PolesCount=2 KnotsCount=2 Degree=1 IsPeriodic=0
    g177: BSplineCurve PolesCount=2 KnotsCount=2 Degree=1 IsPeriodic=0
    g178: BSplineCurve PolesCount=2 KnotsCount=2 Degree=1 IsPeriodic=0
    g179: BSplineCurve PolesCount=2 KnotsCount=2 Degree=1 IsPeriodic=0
    g180: BSplineCurve PolesCount=2 KnotsCount=2 Degree=1 IsPeriodic=0
    g181: BSplineCurve PolesCount=2 KnotsCount=2 Degree=1 IsPeriodic=0
    g182: BSplineCurve PolesCount=2 KnotsCount=2 Degree=1 IsPeriodic=0
    g183: BSplineCurve PolesCount=2 KnotsCount=2 Degree=1 IsPeriodic=0
    g184: BSplineCurve PolesCount=2 KnotsCount=2 Degree=1 IsPeriodic=0
    g185: BSplineCurve PolesCount=2 KnotsCount=2 Degree=1 IsPeriodic=0
    g186: BSplineCurve PolesCount=2 KnotsCount=2 Degree=1 IsPeriodic=0
    g187: BSplineCurve PolesCount=2 KnotsCount=2 Degree=1 IsPeriodic=0
    g188: BSplineCurve PolesCount=2 KnotsCount=2 Degree=1 IsPeriodic=0
    g189: BSplineCurve PolesCount=2 KnotsCount=2 Degree=1 IsPeriodic=0
    g190: BSplineCurve PolesCount=2 KnotsCount=2 Degree=1 IsPeriodic=0
    g191: BSplineCurve PolesCount=2 KnotsCount=2 Degree=1 IsPeriodic=0
    g192: BSplineCurve PolesCount=2 KnotsCount=2 Degree=1 IsPeriodic=0
    g193: BSplineCurve PolesCount=2 KnotsCount=2 Degree=1 IsPeriodic=0
    g194: BSplineCurve PolesCount=2 KnotsCount=2 Degree=1 IsPeriodic=0
    g195: BSplineCurve PolesCount=2 KnotsCount=2 Degree=1 IsPeriodic=0
    g196: BSplineCurve PolesCount=2 KnotsCount=2 Degree=1 IsPeriodic=0
    g197: BSplineCurve PolesCount=2 KnotsCount=2 Degree=1 IsPeriodic=0
    g198: BSplineCurve PolesCount=2 KnotsCount=2 Degree=1 IsPeriodic=0
    g199: BSplineCurve PolesCount=2 KnotsCount=2 Degree=1 IsPeriodic=0
    g200: BSplineCurve PolesCount=2 KnotsCount=2 Degree=1 IsPeriodic=0
    g201: BSplineCurve PolesCount=2 KnotsCount=2 Degree=1 IsPeriodic=0
    g202: BSplineCurve PolesCount=2 KnotsCount=2 Degree=1 IsPeriodic=0
    g203: BSplineCurve PolesCount=2 KnotsCount=2 Degree=1 IsPeriodic=0
    g204: BSplineCurve PolesCount=2 KnotsCount=2 Degree=1 IsPeriodic=0
    g205: BSplineCurve PolesCount=2 KnotsCount=2 Degree=1 IsPeriodic=0
    g206: BSplineCurve PolesCount=2 KnotsCount=2 Degree=1 IsPeriodic=0
    g207: BSplineCurve PolesCount=2 KnotsCount=2 Degree=1 IsPeriodic=0
    g208: BSplineCurve PolesCount=2 KnotsCount=2 Degree=1 IsPeriodic=0
    g209: BSplineCurve PolesCount=2 KnotsCount=2 Degree=1 IsPeriodic=0
    g210: BSplineCurve PolesCount=2 KnotsCount=2 Degree=1 IsPeriodic=0
    g211: BSplineCurve PolesCount=2 KnotsCount=2 Degree=1 IsPeriodic=0
    g212: BSplineCurve PolesCount=2 KnotsCount=2 Degree=1 IsPeriodic=0
    g213: BSplineCurve PolesCount=2 KnotsCount=2 Degree=1 IsPeriodic=0
    g214: BSplineCurve PolesCount=2 KnotsCount=2 Degree=1 IsPeriodic=0
    g215: BSplineCurve PolesCount=2 KnotsCount=2 Degree=1 IsPeriodic=0
    g216: BSplineCurve PolesCount=2 KnotsCount=2 Degree=1 IsPeriodic=0
    g217: BSplineCurve PolesCount=2 KnotsCount=2 Degree=1 IsPeriodic=0
    g218: BSplineCurve PolesCount=2 KnotsCount=2 Degree=1 IsPeriodic=0
    g219: BSplineCurve PolesCount=2 KnotsCount=2 Degree=1 IsPeriodic=0
    g220: BSplineCurve PolesCount=2 KnotsCount=2 Degree=1 IsPeriodic=0
    g221: BSplineCurve PolesCount=2 KnotsCount=2 Degree=1 IsPeriodic=0
    g222: BSplineCurve PolesCount=2 KnotsCount=2 Degree=1 IsPeriodic=0
    g223: BSplineCurve PolesCount=2 KnotsCount=2 Degree=1 IsPeriodic=0
    g224: BSplineCurve PolesCount=2 KnotsCount=2 Degree=1 IsPeriodic=0
    g225: BSplineCurve PolesCount=2 KnotsCount=2 Degree=1 IsPeriodic=0
    g226: BSplineCurve PolesCount=2 KnotsCount=2 Degree=1 IsPeriodic=0
    g227: BSplineCurve PolesCount=2 KnotsCount=2 Degree=1 IsPeriodic=0
    g228: BSplineCurve PolesCount=2 KnotsCount=2 Degree=1 IsPeriodic=0
    g229: BSplineCurve PolesCount=2 KnotsCount=2 Degree=1 IsPeriodic=0
    g230: BSplineCurve PolesCount=2 KnotsCount=2 Degree=1 IsPeriodic=0
    g231: BSplineCurve PolesCount=2 KnotsCount=2 Degree=1 IsPeriodic=0
    g232: BSplineCurve PolesCount=2 KnotsCount=2 Degree=1 IsPeriodic=0
    g233: BSplineCurve PolesCount=2 KnotsCount=2 Degree=1 IsPeriodic=0
    g234: BSplineCurve PolesCount=2 KnotsCount=2 Degree=1 IsPeriodic=0
    g235: BSplineCurve PolesCount=2 KnotsCount=2 Degree=1 IsPeriodic=0
    g236: BSplineCurve PolesCount=2 KnotsCount=2 Degree=1 IsPeriodic=0
    g237: BSplineCurve PolesCount=2 KnotsCount=2 Degree=1 IsPeriodic=0
    g238: BSplineCurve PolesCount=2 KnotsCount=2 Degree=1 IsPeriodic=0
    g239: BSplineCurve PolesCount=2 KnotsCount=2 Degree=1 IsPeriodic=0
    g240: BSplineCurve PolesCount=2 KnotsCount=2 Degree=1 IsPeriodic=0
    g241: BSplineCurve PolesCount=2 KnotsCount=2 Degree=1 IsPeriodic=0
    g242: BSplineCurve PolesCount=2 KnotsCount=2 Degree=1 IsPeriodic=0
    g243: BSplineCurve PolesCount=2 KnotsCount=2 Degree=1 IsPeriodic=0
    g244: BSplineCurve PolesCount=2 KnotsCount=2 Degree=1 IsPeriodic=0
    g245: BSplineCurve PolesCount=2 KnotsCount=2 Degree=1 IsPeriodic=0
    g246: BSplineCurve PolesCount=2 KnotsCount=2 Degree=1 IsPeriodic=0
    g247: BSplineCurve PolesCount=2 KnotsCount=2 Degree=1 IsPeriodic=0
    g248: BSplineCurve PolesCount=2 KnotsCount=2 Degree=1 IsPeriodic=0
    g249: BSplineCurve PolesCount=2 KnotsCount=2 Degree=1 IsPeriodic=0
    g250: BSplineCurve PolesCount=2 KnotsCount=2 Degree=1 IsPeriodic=0
    g251: BSplineCurve PolesCount=2 KnotsCount=2 Degree=1 IsPeriodic=0
    g252: BSplineCurve PolesCount=2 KnotsCount=2 Degree=1 IsPeriodic=0
    g253: BSplineCurve PolesCount=2 KnotsCount=2 Degree=1 IsPeriodic=0
    g254: BSplineCurve PolesCount=2 KnotsCount=2 Degree=1 IsPeriodic=0
    g255: BSplineCurve PolesCount=2 KnotsCount=2 Degree=1 IsPeriodic=0
    g256: BSplineCurve PolesCount=2 KnotsCount=2 Degree=1 IsPeriodic=0
    g257: BSplineCurve PolesCount=2 KnotsCount=2 Degree=1 IsPeriodic=0
    g258: BSplineCurve PolesCount=2 KnotsCount=2 Degree=1 IsPeriodic=0
    g259: BSplineCurve PolesCount=2 KnotsCount=2 Degree=1 IsPeriodic=0
    g260: BSplineCurve PolesCount=2 KnotsCount=2 Degree=1 IsPeriodic=0
    g261: BSplineCurve PolesCount=2 KnotsCount=2 Degree=1 IsPeriodic=0
    g262: BSplineCurve PolesCount=2 KnotsCount=2 Degree=1 IsPeriodic=0
    g263: BSplineCurve PolesCount=2 KnotsCount=2 Degree=1 IsPeriodic=0
    g264: BSplineCurve PolesCount=2 KnotsCount=2 Degree=1 IsPeriodic=0
    g265: BSplineCurve PolesCount=2 KnotsCount=2 Degree=1 IsPeriodic=0
    g266: BSplineCurve PolesCount=2 KnotsCount=2 Degree=1 IsPeriodic=0
    g267: BSplineCurve PolesCount=2 KnotsCount=2 Degree=1 IsPeriodic=0
    g268: BSplineCurve PolesCount=2 KnotsCount=2 Degree=1 IsPeriodic=0
    g269: BSplineCurve PolesCount=2 KnotsCount=2 Degree=1 IsPeriodic=0
    g270: BSplineCurve PolesCount=2 KnotsCount=2 Degree=1 IsPeriodic=0
    g271: BSplineCurve PolesCount=2 KnotsCount=2 Degree=1 IsPeriodic=0
    g272: BSplineCurve PolesCount=2 KnotsCount=2 Degree=1 IsPeriodic=0
    g273: BSplineCurve PolesCount=2 KnotsCount=2 Degree=1 IsPeriodic=0
    g274: BSplineCurve PolesCount=2 KnotsCount=2 Degree=1 IsPeriodic=0
    g275: BSplineCurve PolesCount=2 KnotsCount=2 Degree=1 IsPeriodic=0
    g276: BSplineCurve PolesCount=2 KnotsCount=2 Degree=1 IsPeriodic=0
    g277: BSplineCurve PolesCount=2 KnotsCount=2 Degree=1 IsPeriodic=0
    g278: BSplineCurve PolesCount=2 KnotsCount=2 Degree=1 IsPeriodic=0
    g279: BSplineCurve PolesCount=2 KnotsCount=2 Degree=1 IsPeriodic=0
    g280: BSplineCurve PolesCount=2 KnotsCount=2 Degree=1 IsPeriodic=0
    g281: BSplineCurve PolesCount=2 KnotsCount=2 Degree=1 IsPeriodic=0
    g282: BSplineCurve PolesCount=2 KnotsCount=2 Degree=1 IsPeriodic=0
    g283: BSplineCurve PolesCount=2 KnotsCount=2 Degree=1 IsPeriodic=0
    g284: BSplineCurve PolesCount=2 KnotsCount=2 Degree=1 IsPeriodic=0
    g285: BSplineCurve PolesCount=2 KnotsCount=2 Degree=1 IsPeriodic=0
    g286: BSplineCurve PolesCount=2 KnotsCount=2 Degree=1 IsPeriodic=0
    g287: BSplineCurve PolesCount=2 KnotsCount=2 Degree=1 IsPeriodic=0
    g288: BSplineCurve PolesCount=2 KnotsCount=2 Degree=1 IsPeriodic=0
    g289: BSplineCurve PolesCount=2 KnotsCount=2 Degree=1 IsPeriodic=0
    g290: BSplineCurve PolesCount=2 KnotsCount=2 Degree=1 IsPeriodic=0
    g291: BSplineCurve PolesCount=2 KnotsCount=2 Degree=1 IsPeriodic=0
    g292: BSplineCurve PolesCount=2 KnotsCount=2 Degree=1 IsPeriodic=0
    g293: BSplineCurve PolesCount=2 KnotsCount=2 Degree=1 IsPeriodic=0
    g294: BSplineCurve PolesCount=2 KnotsCount=2 Degree=1 IsPeriodic=0
    g295: BSplineCurve PolesCount=2 KnotsCount=2 Degree=1 IsPeriodic=0
    g296: BSplineCurve PolesCount=2 KnotsCount=2 Degree=1 IsPeriodic=0
    g297: BSplineCurve PolesCount=2 KnotsCount=2 Degree=1 IsPeriodic=0
    g298: BSplineCurve PolesCount=2 KnotsCount=2 Degree=1 IsPeriodic=0
    g299: BSplineCurve PolesCount=2 KnotsCount=2 Degree=1 IsPeriodic=0
    g300: BSplineCurve PolesCount=2 KnotsCount=2 Degree=1 IsPeriodic=0
    g301: BSplineCurve PolesCount=2 KnotsCount=2 Degree=1 IsPeriodic=0
    g302: BSplineCurve PolesCount=2 KnotsCount=2 Degree=1 IsPeriodic=0
    g303: BSplineCurve PolesCount=2 KnotsCount=2 Degree=1 IsPeriodic=0
    g304: BSplineCurve PolesCount=2 KnotsCount=2 Degree=1 IsPeriodic=0
    g305: BSplineCurve PolesCount=2 KnotsCount=2 Degree=1 IsPeriodic=0
    g306: BSplineCurve PolesCount=2 KnotsCount=2 Degree=1 IsPeriodic=0
    g307: BSplineCurve PolesCount=2 KnotsCount=2 Degree=1 IsPeriodic=0
    g308: BSplineCurve PolesCount=2 KnotsCount=2 Degree=1 IsPeriodic=0
    g309: BSplineCurve PolesCount=2 KnotsCount=2 Degree=1 IsPeriodic=0
    g310: BSplineCurve PolesCount=2 KnotsCount=2 Degree=1 IsPeriodic=0
    g311: BSplineCurve PolesCount=2 KnotsCount=2 Degree=1 IsPeriodic=0
    g312: BSplineCurve PolesCount=2 KnotsCount=2 Degree=1 IsPeriodic=0
    g313: BSplineCurve PolesCount=2 KnotsCount=2 Degree=1 IsPeriodic=0
    g314: BSplineCurve PolesCount=2 KnotsCount=2 Degree=1 IsPeriodic=0
    g315: BSplineCurve PolesCount=2 KnotsCount=2 Degree=1 IsPeriodic=0
    g316: BSplineCurve PolesCount=2 KnotsCount=2 Degree=1 IsPeriodic=0
    g317: BSplineCurve PolesCount=2 KnotsCount=2 Degree=1 IsPeriodic=0
    g318: BSplineCurve PolesCount=2 KnotsCount=2 Degree=1 IsPeriodic=0
    g319: BSplineCurve PolesCount=2 KnotsCount=2 Degree=1 IsPeriodic=0
    g320: BSplineCurve PolesCount=2 KnotsCount=2 Degree=1 IsPeriodic=0
    g321: BSplineCurve PolesCount=2 KnotsCount=2 Degree=1 IsPeriodic=0
    g322: BSplineCurve PolesCount=2 KnotsCount=2 Degree=1 IsPeriodic=0
    g323: BSplineCurve PolesCount=2 KnotsCount=2 Degree=1 IsPeriodic=0
    g324: BSplineCurve PolesCount=2 KnotsCount=2 Degree=1 IsPeriodic=0
    g325: BSplineCurve PolesCount=2 KnotsCount=2 Degree=1 IsPeriodic=0
    g326: BSplineCurve PolesCount=2 KnotsCount=2 Degree=1 IsPeriodic=0
    g327: BSplineCurve PolesCount=2 KnotsCount=2 Degree=1 IsPeriodic=0
    g328: BSplineCurve PolesCount=2 KnotsCount=2 Degree=1 IsPeriodic=0
    g329: BSplineCurve PolesCount=2 KnotsCount=2 Degree=1 IsPeriodic=0
    g330: BSplineCurve PolesCount=2 KnotsCount=2 Degree=1 IsPeriodic=0
    g331: BSplineCurve PolesCount=2 KnotsCount=2 Degree=1 IsPeriodic=0
    g332: BSplineCurve PolesCount=2 KnotsCount=2 Degree=1 IsPeriodic=0
    g333: BSplineCurve PolesCount=2 KnotsCount=2 Degree=1 IsPeriodic=0
    g334: BSplineCurve PolesCount=2 KnotsCount=2 Degree=1 IsPeriodic=0
    g335: BSplineCurve PolesCount=2 KnotsCount=2 Degree=1 IsPeriodic=0
    g336: BSplineCurve PolesCount=2 KnotsCount=2 Degree=1 IsPeriodic=0
    g337: BSplineCurve PolesCount=2 KnotsCount=2 Degree=1 IsPeriodic=0
    g338: BSplineCurve PolesCount=2 KnotsCount=2 Degree=1 IsPeriodic=0
    g339: BSplineCurve PolesCount=2 KnotsCount=2 Degree=1 IsPeriodic=0
    g340: BSplineCurve PolesCount=2 KnotsCount=2 Degree=1 IsPeriodic=0
    g341: BSplineCurve PolesCount=2 KnotsCount=2 Degree=1 IsPeriodic=0
    g342: BSplineCurve PolesCount=2 KnotsCount=2 Degree=1 IsPeriodic=0
    g343: BSplineCurve PolesCount=2 KnotsCount=2 Degree=1 IsPeriodic=0
    g344: BSplineCurve PolesCount=2 KnotsCount=2 Degree=1 IsPeriodic=0
    g345: BSplineCurve PolesCount=2 KnotsCount=2 Degree=1 IsPeriodic=0
    g346: BSplineCurve PolesCount=2 KnotsCount=2 Degree=1 IsPeriodic=0
    g347: BSplineCurve PolesCount=2 KnotsCount=2 Degree=1 IsPeriodic=0
    g348: BSplineCurve PolesCount=2 KnotsCount=2 Degree=1 IsPeriodic=0
    g349: BSplineCurve PolesCount=2 KnotsCount=2 Degree=1 IsPeriodic=0
    g350: BSplineCurve PolesCount=2 KnotsCount=2 Degree=1 IsPeriodic=0
    g351: BSplineCurve PolesCount=2 KnotsCount=2 Degree=1 IsPeriodic=0
    g352: BSplineCurve PolesCount=2 KnotsCount=2 Degree=1 IsPeriodic=0
    g353: BSplineCurve PolesCount=2 KnotsCount=2 Degree=1 IsPeriodic=0
    g354: BSplineCurve PolesCount=2 KnotsCount=2 Degree=1 IsPeriodic=0
    g355: BSplineCurve PolesCount=2 KnotsCount=2 Degree=1 IsPeriodic=0
    g356: BSplineCurve PolesCount=2 KnotsCount=2 Degree=1 IsPeriodic=0
    g357: BSplineCurve PolesCount=2 KnotsCount=2 Degree=1 IsPeriodic=0
    g358: BSplineCurve PolesCount=2 KnotsCount=2 Degree=1 IsPeriodic=0
    g359: BSplineCurve PolesCount=2 KnotsCount=2 Degree=1 IsPeriodic=0
    g360: BSplineCurve PolesCount=2 KnotsCount=2 Degree=1 IsPeriodic=0
    g361: BSplineCurve PolesCount=2 KnotsCount=2 Degree=1 IsPeriodic=0
    g362: BSplineCurve PolesCount=2 KnotsCount=2 Degree=1 IsPeriodic=0
    g363: BSplineCurve PolesCount=2 KnotsCount=2 Degree=1 IsPeriodic=0
    g364: BSplineCurve PolesCount=2 KnotsCount=2 Degree=1 IsPeriodic=0
    g365: BSplineCurve PolesCount=2 KnotsCount=2 Degree=1 IsPeriodic=0
    g366: BSplineCurve PolesCount=2 KnotsCount=2 Degree=1 IsPeriodic=0
    g367: BSplineCurve PolesCount=2 KnotsCount=2 Degree=1 IsPeriodic=0
    g368: BSplineCurve PolesCount=2 KnotsCount=2 Degree=1 IsPeriodic=0
    g369: BSplineCurve PolesCount=2 KnotsCount=2 Degree=1 IsPeriodic=0
    g370: BSplineCurve PolesCount=2 KnotsCount=2 Degree=1 IsPeriodic=0
    g371: BSplineCurve PolesCount=2 KnotsCount=2 Degree=1 IsPeriodic=0
    g372: BSplineCurve PolesCount=2 KnotsCount=2 Degree=1 IsPeriodic=0
    g373: BSplineCurve PolesCount=2 KnotsCount=2 Degree=1 IsPeriodic=0
    g374: BSplineCurve PolesCount=2 KnotsCount=2 Degree=1 IsPeriodic=0
    g375: BSplineCurve PolesCount=2 KnotsCount=2 Degree=1 IsPeriodic=0
    g376: BSplineCurve PolesCount=2 KnotsCount=2 Degree=1 IsPeriodic=0
    g377: BSplineCurve PolesCount=2 KnotsCount=2 Degree=1 IsPeriodic=0
    g378: BSplineCurve PolesCount=2 KnotsCount=2 Degree=1 IsPeriodic=0
    g379: BSplineCurve PolesCount=2 KnotsCount=2 Degree=1 IsPeriodic=0
    g380: BSplineCurve PolesCount=2 KnotsCount=2 Degree=1 IsPeriodic=0
    g381: BSplineCurve PolesCount=2 KnotsCount=2 Degree=1 IsPeriodic=0
    g382: BSplineCurve PolesCount=2 KnotsCount=2 Degree=1 IsPeriodic=0
    g383: BSplineCurve PolesCount=2 KnotsCount=2 Degree=1 IsPeriodic=0
    g384: BSplineCurve PolesCount=2 KnotsCount=2 Degree=1 IsPeriodic=0
    g385: BSplineCurve PolesCount=2 KnotsCount=2 Degree=1 IsPeriodic=0
    g386: BSplineCurve PolesCount=2 KnotsCount=2 Degree=1 IsPeriodic=0
    g387: BSplineCurve PolesCount=2 KnotsCount=2 Degree=1 IsPeriodic=0
    g388: BSplineCurve PolesCount=2 KnotsCount=2 Degree=1 IsPeriodic=0
    g389: BSplineCurve PolesCount=2 KnotsCount=2 Degree=1 IsPeriodic=0
    g390: BSplineCurve PolesCount=2 KnotsCount=2 Degree=1 IsPeriodic=0
    g391: BSplineCurve PolesCount=2 KnotsCount=2 Degree=1 IsPeriodic=0
    g392: BSplineCurve PolesCount=2 KnotsCount=2 Degree=1 IsPeriodic=0
    g393: BSplineCurve PolesCount=2 KnotsCount=2 Degree=1 IsPeriodic=0
    g394: BSplineCurve PolesCount=2 KnotsCount=2 Degree=1 IsPeriodic=0
    g395: BSplineCurve PolesCount=2 KnotsCount=2 Degree=1 IsPeriodic=0
    g396: BSplineCurve PolesCount=2 KnotsCount=2 Degree=1 IsPeriodic=0
    g397: BSplineCurve PolesCount=2 KnotsCount=2 Degree=1 IsPeriodic=0
    g398: BSplineCurve PolesCount=2 KnotsCount=2 Degree=1 IsPeriodic=0
    g399: BSplineCurve PolesCount=2 KnotsCount=2 Degree=1 IsPeriodic=0
    ... +4 more geometry lines
  constraints (412):
    c: Coincident(g0,g1)
    c: Coincident(g1,g2)
    c: Coincident(g2,g3)
    c: Coincident(g3,g4)
    c: Coincident(g4,g5)
    c: Coincident(g5,g6)
    c: Coincident(g6,g7)
    c: Coincident(g7,g8)
    c: Coincident(g8,g9)
    c: Coincident(g9,g10)
    c: Coincident(g10,g11)
    c: Coincident(g11,g12)
    c: Coincident(g12,g13)
    c: Coincident(g13,g14)
    c: Coincident(g14,g15)
    c: Coincident(g15,g16)
    c: Coincident(g16,g17)
    c: Coincident(g17,g18)
    c: Coincident(g18,g19)
    c: Coincident(g19,g0)
    c: Coincident(g20,g21)
    c: Coincident(g21,g22)
    c: Coincident(g22,g23)
    c: Coincident(g23,g24)
    c: Coincident(g24,g25)
    c: Coincident(g25,g26)
    c: Coincident(g26,g27)
    c: Coincident(g27,g28)
    c: Coincident(g28,g29)
    c: Coincident(g29,g30)
    c: Coincident(g30,g31)
    c: Coincident(g31,g32)
    c: Coincident(g32,g33)
    c: Coincident(g33,g34)
    c: Coincident(g34,g35)
    c: Coincident(g35,g36)
    c: Coincident(g36,g37)
    c: Coincident(g37,g38)
    c: Coincident(g38,g39)
    c: Coincident(g39,g20)
    c: Coincident(g40,g41)
    c: Coincident(g41,g42)
    c: Coincident(g42,g43)
    c: Coincident(g43,g44)
    c: Coincident(g44,g45)
    c: Coincident(g45,g46)
    c: Coincident(g46,g47)
    c: Coincident(g47,g48)
    c: Coincident(g48,g49)
    c: Coincident(g49,g50)
    c: Coincident(g50,g51)
    c: Coincident(g51,g52)
    c: Coincident(g52,g53)
    c: Coincident(g53,g54)
    c: Coincident(g54,g55)
    c: Coincident(g55,g56)
    c: Coincident(g56,g57)
    c: Coincident(g57,g58)
    c: Coincident(g58,g59)
    c: Coincident(g59,g40)
    c: Coincident(g60,g61)
    c: Coincident(g61,g62)
    c: Coincident(g62,g63)
    c: Coincident(g63,g64)
    c: Coincident(g64,g65)
    c: Coincident(g65,g66)
    c: Coincident(g66,g67)
    c: Coincident(g67,g68)
    c: Coincident(g68,g69)
    c: Coincident(g69,g70)
    c: Coincident(g70,g71)
    c: Coincident(g71,g72)
    c: Coincident(g72,g73)
    c: Coincident(g73,g74)
    c: Coincident(g74,g75)
    c: Coincident(g75,g76)
    c: Coincident(g76,g77)
    c: Coincident(g77,g78)
    c: Coincident(g78,g79)
    c: Coincident(g79,g60)
    c: Coincident(g80,g81)
    c: Coincident(g81,g82)
    c: Coincident(g82,g83)
    c: Coincident(g83,g84)
    c: Coincident(g84,g85)
    c: Coincident(g85,g86)
    c: Coincident(g86,g87)
    c: Coincident(g87,g88)
    c: Coincident(g88,g89)
    c: Coincident(g89,g90)
    c: Coincident(g90,g91)
    c: Coincident(g91,g92)
    c: Coincident(g92,g93)
    c: Coincident(g93,g94)
    c: Coincident(g94,g95)
    c: Coincident(g95,g96)
    c: Coincident(g96,g97)
    c: Coincident(g97,g98)
    c: Coincident(g98,g99)
    c: Coincident(g99,g80)
    c: Coincident(g100,g101)
    c: Coincident(g101,g102)
    c: Coincident(g102,g103)
    c: Coincident(g103,g104)
    c: Coincident(g104,g105)
    c: Coincident(g105,g106)
    c: Coincident(g106,g107)
    c: Coincident(g107,g108)
    c: Coincident(g108,g109)
    c: Coincident(g109,g110)
    c: Coincident(g110,g111)
    c: Coincident(g111,g112)
    c: Coincident(g112,g113)
    c: Coincident(g113,g114)
    c: Coincident(g114,g115)
    c: Coincident(g115,g116)
    c: Coincident(g116,g117)
    c: Coincident(g117,g118)
    c: Coincident(g118,g119)
    c: Coincident(g119,g100)
    c: Coincident(g120,g121)
    c: Coincident(g121,g122)
    c: Coincident(g122,g123)
    c: Coincident(g123,g124)
    c: Coincident(g124,g125)
    c: Coincident(g125,g126)
    c: Coincident(g126,g127)
    c: Coincident(g127,g128)
    c: Coincident(g128,g129)
    c: Coincident(g129,g130)
    c: Coincident(g130,g131)
    c: Coincident(g131,g132)
    c: Coincident(g132,g133)
    c: Coincident(g133,g134)
    c: Coincident(g134,g135)
    c: Coincident(g135,g136)
    c: Coincident(g136,g137)
    c: Coincident(g137,g138)
    c: Coincident(g138,g139)
    c: Coincident(g139,g120)
    c: Coincident(g140,g141)
    c: Coincident(g141,g142)
    c: Coincident(g142,g143)
    c: Coincident(g143,g144)
    c: Coincident(g144,g145)
    c: Coincident(g145,g146)
    c: Coincident(g146,g147)
    c: Coincident(g147,g148)
    c: Coincident(g148,g149)
    c: Coincident(g149,g150)
    c: Coincident(g150,g151)
    c: Coincident(g151,g152)
    c: Coincident(g152,g153)
    c: Coincident(g153,g154)
    c: Coincident(g154,g155)
    c: Coincident(g155,g156)
    c: Coincident(g156,g157)
    c: Coincident(g157,g158)
    c: Coincident(g158,g159)
    c: Coincident(g159,g140)
    c: Coincident(g160,g161)
    c: Coincident(g161,g162)
    c: Coincident(g162,g163)
    c: Coincident(g163,g164)
    c: Coincident(g164,g165)
    c: Coincident(g165,g166)
    c: Coincident(g166,g167)
    c: Coincident(g167,g168)
    c: Coincident(g168,g169)
    c: Coincident(g169,g170)
    c: Coincident(g170,g171)
    c: Coincident(g171,g172)
    c: Coincident(g172,g173)
    c: Coincident(g173,g174)
    c: Coincident(g174,g175)
    c: Coincident(g175,g176)
    c: Coincident(g176,g177)
    c: Coincident(g177,g178)
    c: Coincident(g178,g179)
    c: Coincident(g179,g160)
    c: Coincident(g180,g181)
    c: Coincident(g181,g182)
    c: Coincident(g182,g183)
    c: Coincident(g183,g184)
    c: Coincident(g184,g185)
    c: Coincident(g185,g186)
    c: Coincident(g186,g187)
    c: Coincident(g187,g188)
    c: Coincident(g188,g189)
    c: Coincident(g189,g190)
    c: Coincident(g190,g191)
    c: Coincident(g191,g192)
    c: Coincident(g192,g193)
    c: Coincident(g193,g194)
    c: Coincident(g194,g195)
    c: Coincident(g195,g196)
    c: Coincident(g196,g197)
    c: Coincident(g197,g198)
    c: Coincident(g198,g199)
    c: Coincident(g199,g180)
    c: Coincident(g200,g201)
    c: Coincident(g201,g202)
    c: Coincident(g202,g203)
    c: Coincident(g203,g204)
    c: Coincident(g204,g205)
    c: Coincident(g205,g206)
    c: Coincident(g206,g207)
    c: Coincident(g207,g208)
    c: Coincident(g208,g209)
    c: Coincident(g209,g210)
    c: Coincident(g210,g211)
    c: Coincident(g211,g212)
    c: Coincident(g212,g213)
    c: Coincident(g213,g214)
    c: Coincident(g214,g215)
    c: Coincident(g215,g216)
    c: Coincident(g216,g217)
    c: Coincident(g217,g218)
    c: Coincident(g218,g219)
    c: Coincident(g219,g200)
    c: Coincident(g220,g221)
    c: Coincident(g221,g222)
    c: Coincident(g222,g223)
    c: Coincident(g223,g224)
    c: Coincident(g224,g225)
    c: Coincident(g225,g226)
    c: Coincident(g226,g227)
    c: Coincident(g227,g228)
    c: Coincident(g228,g229)
    c: Coincident(g229,g230)
    c: Coincident(g230,g231)
    c: Coincident(g231,g232)
    c: Coincident(g232,g233)
    c: Coincident(g233,g234)
    c: Coincident(g234,g235)
    c: Coincident(g235,g236)
    c: Coincident(g236,g237)
    c: Coincident(g237,g238)
    c: Coincident(g238,g239)
    c: Coincident(g239,g220)
    c: Coincident(g240,g241)
    c: Coincident(g241,g242)
    c: Coincident(g242,g243)
    c: Coincident(g243,g244)
    c: Coincident(g244,g245)
    c: Coincident(g245,g246)
    c: Coincident(g246,g247)
    c: Coincident(g247,g248)
    c: Coincident(g248,g249)
    c: Coincident(g249,g250)
    c: Coincident(g250,g251)
    c: Coincident(g251,g252)
    c: Coincident(g252,g253)
    c: Coincident(g253,g254)
    c: Coincident(g254,g255)
    c: Coincident(g255,g256)
    c: Coincident(g256,g257)
    c: Coincident(g257,g258)
    c: Coincident(g258,g259)
    c: Coincident(g259,g240)
    c: Coincident(g260,g261)
    c: Coincident(g261,g262)
    c: Coincident(g262,g263)
    c: Coincident(g263,g264)
    c: Coincident(g264,g265)
    c: Coincident(g265,g266)
    c: Coincident(g266,g267)
    c: Coincident(g267,g268)
    c: Coincident(g268,g269)
    c: Coincident(g269,g270)
    c: Coincident(g270,g271)
    c: Coincident(g271,g272)
    c: Coincident(g272,g273)
    c: Coincident(g273,g274)
    c: Coincident(g274,g275)
    c: Coincident(g275,g276)
    c: Coincident(g276,g277)
    c: Coincident(g277,g278)
    c: Coincident(g278,g279)
    c: Coincident(g279,g260)
    c: Coincident(g280,g281)
    c: Coincident(g281,g282)
    c: Coincident(g282,g283)
    c: Coincident(g283,g284)
    c: Coincident(g284,g285)
    c: Coincident(g285,g286)
    c: Coincident(g286,g287)
    c: Coincident(g287,g288)
    c: Coincident(g288,g289)
    c: Coincident(g289,g290)
    c: Coincident(g290,g291)
    c: Coincident(g291,g292)
    c: Coincident(g292,g293)
    c: Coincident(g293,g294)
    c: Coincident(g294,g295)
    c: Coincident(g295,g296)
    c: Coincident(g296,g297)
    c: Coincident(g297,g298)
    c: Coincident(g298,g299)
    c: Coincident(g299,g280)
    c: Coincident(g300,g301)
    c: Coincident(g301,g302)
    c: Coincident(g302,g303)
    c: Coincident(g303,g304)
    c: Coincident(g304,g305)
    c: Coincident(g305,g306)
    c: Coincident(g306,g307)
    c: Coincident(g307,g308)
    c: Coincident(g308,g309)
    c: Coincident(g309,g310)
    c: Coincident(g310,g311)
    c: Coincident(g311,g312)
    c: Coincident(g312,g313)
    c: Coincident(g313,g314)
    c: Coincident(g314,g315)
    c: Coincident(g315,g316)
    c: Coincident(g316,g317)
    c: Coincident(g317,g318)
    c: Coincident(g318,g319)
    c: Coincident(g319,g300)
    c: Coincident(g320,g321)
    c: Coincident(g321,g322)
    c: Coincident(g322,g323)
    c: Coincident(g323,g324)
    c: Coincident(g324,g325)
    c: Coincident(g325,g326)
    c: Coincident(g326,g327)
    c: Coincident(g327,g328)
    c: Coincident(g328,g329)
    c: Coincident(g329,g330)
    c: Coincident(g330,g331)
    c: Coincident(g331,g332)
    c: Coincident(g332,g333)
    c: Coincident(g333,g334)
    c: Coincident(g334,g335)
    c: Coincident(g335,g336)
    c: Coincident(g336,g337)
    c: Coincident(g337,g338)
    c: Coincident(g338,g339)
    c: Coincident(g339,g320)
    c: Coincident(g340,g341)
    c: Coincident(g341,g342)
    c: Coincident(g342,g343)
    c: Coincident(g343,g344)
    c: Coincident(g344,g345)
    c: Coincident(g345,g346)
    c: Coincident(g346,g347)
    c: Coincident(g347,g348)
    c: Coincident(g348,g349)
    c: Coincident(g349,g350)
    c: Coincident(g350,g351)
    c: Coincident(g351,g352)
    c: Coincident(g352,g353)
    c: Coincident(g353,g354)
    c: Coincident(g354,g355)
    c: Coincident(g355,g356)
    c: Coincident(g356,g357)
    c: Coincident(g357,g358)
    c: Coincident(g358,g359)
    c: Coincident(g359,g340)
    c: Coincident(g360,g361)
    c: Coincident(g361,g362)
    c: Coincident(g362,g363)
    c: Coincident(g363,g364)
    c: Coincident(g364,g365)
    c: Coincident(g365,g366)
    c: Coincident(g366,g367)
    c: Coincident(g367,g368)
    c: Coincident(g368,g369)
    c: Coincident(g369,g370)
    c: Coincident(g370,g371)
    c: Coincident(g371,g372)
    c: Coincident(g372,g373)
    c: Coincident(g373,g374)
    c: Coincident(g374,g375)
    c: Coincident(g375,g376)
    c: Coincident(g376,g377)
    c: Coincident(g377,g378)
    c: Coincident(g378,g379)
    c: Coincident(g379,g360)
    c: Coincident(g380,g381)
    c: Coincident(g381,g382)
    c: Coincident(g382,g383)
    c: Coincident(g383,g384)
    c: Coincident(g384,g385)
    c: Coincident(g385,g386)
    c: Coincident(g386,g387)
    c: Coincident(g387,g388)
    c: Coincident(g388,g389)
    c: Coincident(g389,g390)
    c: Coincident(g390,g391)
    c: Coincident(g391,g392)
    c: Coincident(g392,g393)
    c: Coincident(g393,g394)
    c: Coincident(g394,g395)
    c: Coincident(g395,g396)
    c: Coincident(g396,g397)
    c: Coincident(g397,g398)
    c: Coincident(g398,g399)
    c: Coincident(g399,g380)
    c: Coincident(g400,g401)
    c: Coincident(g401,g402)
    c: Coincident(g402,g403)
    c: Coincident(g403,g400)
    c: Vertical(g400)
    c: Vertical(g402)
    c: Horizontal(g401)
    c: Horizontal(g403)
    c: DistanceY(g402,g402) = 15.6
    c: DistanceX(g403,g403) = 17
    c: DistanceY(g400) = 64.7
    c: DistanceX(g400) = -148.35
FEATURE [Part::Extrusion] Extrude002  label="PCB"
  Base = -> Sketch002
  Dir = (0,0,1)
  DirMode = 2
  FaceMakerClass = Part::FaceMakerBullseye
  FaceMakerMode = 3
  LengthFwd = 0.2
  LengthRev = 0
  Solid = true
  Symmetric = false
FEATURE [Part::MultiFuse] Fusion
  Refine = true
  Shapes = -> [Box,Extrude,Extrude001]
